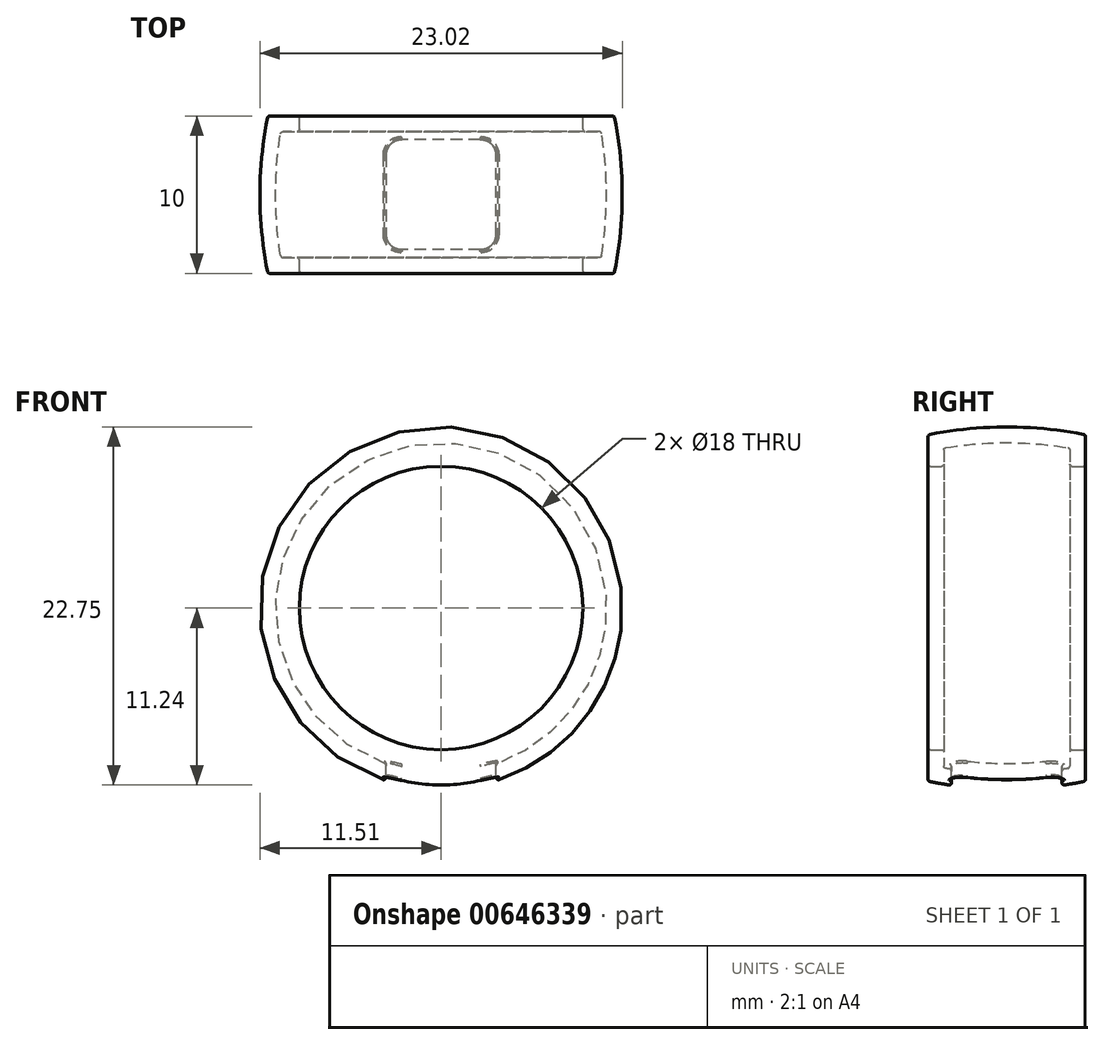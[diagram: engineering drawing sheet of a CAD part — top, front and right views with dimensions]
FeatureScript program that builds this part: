
annotation { "Feature Type Name" : "Feature", "Feature Type Description" : "" }
export const myFeature = defineFeature(function(context is Context, id is Id, definition is map)
    precondition{}
    {
        {
            var Q0;
            Q0=qCreatedBy(makeId("Top.planeOp"),FACE);
            var sketch = newSketch(context, id + "F0", { "sketchPlane" : qUnion([Q0])});
            skLineSegment(sketch, "E0", {"start": v(0, 0) * mm, "end": v(-9, 0) * mm, "construction": true});
            skLineSegment(sketch, "E1", {"start": v(-9, 5) * mm, "end": v(-9, -5) * mm});
            skLineSegment(sketch, "E2", {"start": v(-9, 5) * mm, "end": v(-11, 5) * mm});
            skLineSegment(sketch, "E3", {"start": v(-9, -5) * mm, "end": v(-11, -5) * mm});
            skArc(sketch, "E4", {"start": v(-11, 5) * mm, "mid": v(-11.5, 0) * mm, "end": v(-11, -5) * mm});
            skLineSegment(sketch, "E5", {"start": v(0, 0) * mm, "end": v(0, -17) * mm, "construction": true});
            skSolve(sketch);
        }
        {
            var Q0;
            Q0=makeQuery(id+"F0.imprint","IMPRINT",FACE,{"disambiguationData":[TD([[makeQuery(id+"F0.imprint","IMPRINT",EDGE,{"derivedFrom":sQuery(id+"F0.wireOp",EDGE,"E1")}),-1.0]])]});
            var Q1;
            Q1=sQuery(id+"F0.wireOp",EDGE,"E5");
            revolve(context, id + "F1", {"entities" : qUnion([Q0]), "axis" : qUnion([Q1]), "revolveType" : RevolveType.FULL});
        }
        {
            var Q0;
            Q0=makeQuery(id+"F1.opRevolve","SWEPT_FACE",FACE,{"disambiguationData":[OSD([sQuery(id+"F0.wireOp",EDGE,"E1")])]});
            shell(context, id + "F2", {"entities" : qUnion([Q0]), "thickness" : 1 * mm});
        }
        {
            var Q0;
            Q0=makeQuery(id+"F1.opRevolve","SWEPT_EDGE",EDGE,{"disambiguationData":[OSD([sQuery(id+"F0.wireOp",EDGE,"E1"),sQuery(id+"F0.wireOp",EDGE,"E2")])]});
            var Q1;
            Q1=makeQuery(id+"F1.opRevolve","SWEPT_EDGE",EDGE,{"disambiguationData":[OSD([sQuery(id+"F0.wireOp",EDGE,"E2"),sQuery(id+"F0.wireOp",EDGE,"E4")])]});
            var Q2;
            Q2=makeQuery(id+"F2.opShell","OFFSET_FACE",FACE,{"disambiguationData":[OSD([sQuery(id+"F0.wireOp",EDGE,"E1")])]});
            var Q3;
            Q3=makeQuery(id+"F1.opRevolve","SWEPT_FACE",FACE,{"disambiguationData":[OSD([sQuery(id+"F0.wireOp",EDGE,"E2")])]});
            var Q4;
            Q4=makeQuery(id+"F1.opRevolve","SWEPT_EDGE",EDGE,{"disambiguationData":[OSD([sQuery(id+"F0.wireOp",EDGE,"E3"),sQuery(id+"F0.wireOp",EDGE,"E4")])]});
            var Q5;
            Q5=makeQuery(id+"F2.opShell","OFFSET_EDGE",EDGE,{"disambiguationData":[OSD([sQuery(id+"F0.wireOp",EDGE,"E1"),sQuery(id+"F0.wireOp",EDGE,"E2")])]});
            var Q6;
            Q6=makeQuery(id+"F1.opRevolve","SWEPT_FACE",FACE,{"disambiguationData":[OSD([sQuery(id+"F0.wireOp",EDGE,"E3")])]});
            var Q7;
            Q7=makeQuery(id+"F1.opRevolve","SWEPT_EDGE",EDGE,{"disambiguationData":[OSD([sQuery(id+"F0.wireOp",EDGE,"E1"),sQuery(id+"F0.wireOp",EDGE,"E3")])]});
            var Q8;
            Q8=makeQuery(id+"F2.opShell","OFFSET_EDGE",EDGE,{"disambiguationData":[OSD([sQuery(id+"F0.wireOp",EDGE,"E1"),sQuery(id+"F0.wireOp",EDGE,"E3")])]});
            var Q9;
            Q9=makeQuery(id+"F2.opShell","OFFSET_FACE",FACE,{"disambiguationData":[OSD([sQuery(id+"F0.wireOp",EDGE,"E2")])]});
            var Q10;
            Q10=makeQuery(id+"F2.opShell","OFFSET_EDGE",EDGE,{"disambiguationData":[OSD([sQuery(id+"F0.wireOp",EDGE,"E2"),sQuery(id+"F0.wireOp",EDGE,"E4")])]});
            var Q11;
            Q11=makeQuery(id+"F2.opShell","OFFSET_FACE",FACE,{"disambiguationData":[OSD([sQuery(id+"F0.wireOp",EDGE,"E3")])]});
            var Q12;
            Q12=makeQuery(id+"F2.opShell","OFFSET_EDGE",EDGE,{"disambiguationData":[OSD([sQuery(id+"F0.wireOp",EDGE,"E3"),sQuery(id+"F0.wireOp",EDGE,"E4")])]});
            var Q13;
            Q13=makeQuery(id+"F2.opShell","OFFSET_FACE",FACE,{"disambiguationData":[OSD([sQuery(id+"F0.wireOp",EDGE,"E4")])]});
            var Q14;
            Q14=makeQuery(id+"F1.opRevolve","SWEPT_FACE",FACE,{"disambiguationData":[OSD([sQuery(id+"F0.wireOp",EDGE,"E1")])]});
            var Q15;
            Q15=makeQuery(id+"F1.opRevolve","SWEPT_FACE",FACE,{"disambiguationData":[OSD([sQuery(id+"F0.wireOp",EDGE,"E4")])]});
            fillet(context, id + "F3", {"entities" : qUnion([Q0, Q1, Q2, Q3, Q4, Q5, Q6, Q7, Q8, Q9, Q10, Q11, Q12, Q13, Q14, Q15]), "radius" : 0.15 * mm, "tangentPropagation" : true, "allowEdgeOverflow" : false});
        }
        {
            var Q0;
            Q0=qCreatedBy(makeId("Top.planeOp"),FACE);
            var sketch = newSketch(context, id + "F4", { "sketchPlane" : qUnion([Q0])});
            skLineSegment(sketch, "E6.bottom", {"start": v(2.5, 3.5) * mm, "end": v(-2.5, 3.5) * mm});
            skLineSegment(sketch, "E6.top", {"start": v(2.5, -3.5) * mm, "end": v(-2.5, -3.5) * mm});
            skLineSegment(sketch, "E6.left", {"start": v(3.5, 2.5) * mm, "end": v(3.5, -2.5) * mm});
            skLineSegment(sketch, "E6.right", {"start": v(-3.5, 2.5) * mm, "end": v(-3.5, -2.5) * mm});
            skPoint(sketch, "E6.middle", {"position": v(0, 0) * mm});
            skPoint(sketch, "E7.visualSharp", {"position": v(-3.5, 3.5) * mm});
            skArc(sketch, "E7.filletArc", {"start": v(-2.5, 3.5) * mm, "mid": v(-3.2, 3.2) * mm, "end": v(-3.5, 2.5) * mm});
            skPoint(sketch, "E8.visualSharp", {"position": v(3.5, 3.5) * mm});
            skArc(sketch, "E8.filletArc", {"start": v(3.5, 2.5) * mm, "mid": v(3.2, 3.2) * mm, "end": v(2.5, 3.5) * mm});
            skPoint(sketch, "E9.visualSharp", {"position": v(3.5, -3.5) * mm});
            skArc(sketch, "E9.filletArc", {"start": v(2.5, -3.5) * mm, "mid": v(3.2, -3.2) * mm, "end": v(3.5, -2.5) * mm});
            skPoint(sketch, "E10.visualSharp", {"position": v(-3.5, -3.5) * mm});
            skArc(sketch, "E10.filletArc", {"start": v(-3.5, -2.5) * mm, "mid": v(-3.2, -3.2) * mm, "end": v(-2.5, -3.5) * mm});
            skSolve(sketch);
        }
        {
            var Q0;
            Q0=makeQuery(id+"F4.imprint","IMPRINT",FACE,{"disambiguationData":[TD([[makeQuery(id+"F4.imprint","IMPRINT",EDGE,{"derivedFrom":sQuery(id+"F4.wireOp",EDGE,"E6.bottom")}),1.0]])]});
            extrude(context, id + "F5", {"entities" : qUnion([Q0]), "operationType" : NewBodyOperationType.REMOVE, "endBound" : BoundingType.THROUGH_ALL, "oppositeDirection" : true, "depth" : 25 * mm, "offsetDistance" : 25 * mm});
        }
        {
            var Q0;
            {var subQ0=sQuery(id+"F0.wireOp",EDGE,"E3");var subQ1=sQuery(id+"F0.wireOp",EDGE,"E1");Q0=makeQuery(id+"F3.opFillet","BLEND_FACE",FACE,{"disambiguationData":[OSD([subQ1,subQ0]),TDD([makeQuery(id+"F1.opRevolve","SWEPT_EDGE",EDGE,{"disambiguationData":[OSD([subQ1,subQ0])]})])]});}
            var Q1;
            {var subQ0=sQuery(id+"F0.wireOp",EDGE,"E3");var subQ1=sQuery(id+"F0.wireOp",EDGE,"E1");Q1=makeQuery(id+"F3.opFillet","BLEND_FACE",FACE,{"disambiguationData":[OSD([subQ1,subQ0]),TDD([makeQuery(id+"F2.opShell","OFFSET_EDGE",EDGE,{"disambiguationData":[OSD([subQ1,subQ0])]})])]});}
            var Q2;
            {var subQ0=sQuery(id+"F0.wireOp",EDGE,"E2");var subQ1=sQuery(id+"F0.wireOp",EDGE,"E1");Q2=makeQuery(id+"F3.opFillet","BLEND_FACE",FACE,{"disambiguationData":[OSD([subQ1,subQ0]),TDD([makeQuery(id+"F2.opShell","OFFSET_EDGE",EDGE,{"disambiguationData":[OSD([subQ1,subQ0])]})])]});}
            var Q3;
            {var subQ0=sQuery(id+"F0.wireOp",EDGE,"E1");Q3=makeQuery(id+"F3.opFillet","BLEND_EDGE",EDGE,{"blendedFrom":[makeQuery(id+"F1.opRevolve","SWEPT_EDGE",EDGE,{"disambiguationData":[OSD([subQ0,sQuery(id+"F0.wireOp",EDGE,"E2")])]}),makeQuery(id+"F2.opShell","OFFSET_FACE",FACE,{"disambiguationData":[OSD([subQ0])]})],"blendedInto":[makeQuery(id+"F2.opShell","OFFSET_FACE",FACE,{"disambiguationData":[OSD([subQ0])]})]});}
            var Q4;
            {var subQ0=sQuery(id+"F0.wireOp",EDGE,"E4");Q4=makeQuery(id+"F3.opFillet","BLEND_EDGE",EDGE,{"blendedFrom":[makeQuery(id+"F1.opRevolve","SWEPT_EDGE",EDGE,{"disambiguationData":[OSD([sQuery(id+"F0.wireOp",EDGE,"E2"),subQ0])]}),makeQuery(id+"F1.opRevolve","SWEPT_FACE",FACE,{"disambiguationData":[OSD([subQ0])]})],"blendedInto":[makeQuery(id+"F1.opRevolve","SWEPT_FACE",FACE,{"disambiguationData":[OSD([subQ0])]})]});}
            var Q5;
            {var subQ0=sQuery(id+"F0.wireOp",EDGE,"E4");var subQ1=sQuery(id+"F0.wireOp",EDGE,"E3");Q5=makeQuery(id+"F3.opFillet","BLEND_FACE",FACE,{"disambiguationData":[OSD([subQ1,subQ0]),TDD([makeQuery(id+"F1.opRevolve","SWEPT_EDGE",EDGE,{"disambiguationData":[OSD([subQ1,subQ0])]})])]});}
            var Q6;
            {var subQ0=sQuery(id+"F0.wireOp",EDGE,"E1");Q6=makeQuery(id+"F3.opFillet","BLEND_EDGE",EDGE,{"blendedFrom":[makeQuery(id+"F1.opRevolve","SWEPT_EDGE",EDGE,{"disambiguationData":[OSD([subQ0,sQuery(id+"F0.wireOp",EDGE,"E3")])]}),makeQuery(id+"F1.opRevolve","SWEPT_FACE",FACE,{"disambiguationData":[OSD([subQ0])]})],"blendedInto":[makeQuery(id+"F1.opRevolve","SWEPT_FACE",FACE,{"disambiguationData":[OSD([subQ0])]})]});}
            var Q7;
            {var subQ0=sQuery(id+"F0.wireOp",EDGE,"E4");var subQ1=sQuery(id+"F0.wireOp",EDGE,"E2");Q7=makeQuery(id+"F3.opFillet","BLEND_FACE",FACE,{"disambiguationData":[OSD([subQ1,subQ0]),TDD([makeQuery(id+"F1.opRevolve","SWEPT_EDGE",EDGE,{"disambiguationData":[OSD([subQ1,subQ0])]})])]});}
            var Q8;
            {var subQ0=sQuery(id+"F0.wireOp",EDGE,"E3");Q8=makeQuery(id+"F3.opFillet","BLEND_EDGE",EDGE,{"blendedFrom":[makeQuery(id+"F1.opRevolve","SWEPT_EDGE",EDGE,{"disambiguationData":[OSD([subQ0,sQuery(id+"F0.wireOp",EDGE,"E4")])]}),makeQuery(id+"F1.opRevolve","SWEPT_FACE",FACE,{"disambiguationData":[OSD([subQ0])]})],"blendedInto":[makeQuery(id+"F1.opRevolve","SWEPT_FACE",FACE,{"disambiguationData":[OSD([subQ0])]})]});}
            var Q9;
            {var subQ0=sQuery(id+"F0.wireOp",EDGE,"E3");Q9=makeQuery(id+"F3.opFillet","BLEND_EDGE",EDGE,{"blendedFrom":[makeQuery(id+"F1.opRevolve","SWEPT_EDGE",EDGE,{"disambiguationData":[OSD([sQuery(id+"F0.wireOp",EDGE,"E1"),subQ0])]}),makeQuery(id+"F1.opRevolve","SWEPT_FACE",FACE,{"disambiguationData":[OSD([subQ0])]})],"blendedInto":[makeQuery(id+"F1.opRevolve","SWEPT_FACE",FACE,{"disambiguationData":[OSD([subQ0])]})]});}
            var Q10;
            {var subQ0=sQuery(id+"F0.wireOp",EDGE,"E2");var subQ1=sQuery(id+"F0.wireOp",EDGE,"E1");Q10=makeQuery(id+"F3.opFillet","BLEND_FACE",FACE,{"disambiguationData":[OSD([subQ1,subQ0]),TDD([makeQuery(id+"F1.opRevolve","SWEPT_EDGE",EDGE,{"disambiguationData":[OSD([subQ1,subQ0])]})])]});}
            var Q11;
            {var subQ0=sQuery(id+"F0.wireOp",EDGE,"E4");Q11=makeQuery(id+"F3.opFillet","BLEND_EDGE",EDGE,{"blendedFrom":[makeQuery(id+"F2.opShell","OFFSET_EDGE",EDGE,{"disambiguationData":[OSD([sQuery(id+"F0.wireOp",EDGE,"E2"),subQ0])]}),makeQuery(id+"F2.opShell","OFFSET_FACE",FACE,{"disambiguationData":[OSD([subQ0])]})],"blendedInto":[makeQuery(id+"F2.opShell","OFFSET_FACE",FACE,{"disambiguationData":[OSD([subQ0])]})]});}
            var Q12;
            Q12=makeQuery(id+"F1.opRevolve","SWEPT_FACE",FACE,{"disambiguationData":[OSD([sQuery(id+"F0.wireOp",EDGE,"E1")])]});
            var Q13;
            Q13=makeQuery(id+"F5.boolean.opBoolean","COPY",FACE,{"derivedFrom":makeQuery(id+"F5.opExtrude","SWEPT_FACE",FACE,{"disambiguationData":[OSD([sQuery(id+"F4.wireOp",EDGE,"E10.filletArc")])]})});
            var Q14;
            {var subQ0=sQuery(id+"F0.wireOp",EDGE,"E1");Q14=makeQuery(id+"F3.opFillet","BLEND_EDGE",EDGE,{"blendedFrom":[makeQuery(id+"F2.opShell","OFFSET_EDGE",EDGE,{"disambiguationData":[OSD([subQ0,sQuery(id+"F0.wireOp",EDGE,"E3")])]}),makeQuery(id+"F1.opRevolve","SWEPT_FACE",FACE,{"disambiguationData":[OSD([subQ0])]})],"blendedInto":[makeQuery(id+"F1.opRevolve","SWEPT_FACE",FACE,{"disambiguationData":[OSD([subQ0])]})]});}
            var Q15;
            Q15=makeQuery(id+"F2.opShell","OFFSET_FACE",FACE,{"disambiguationData":[OSD([sQuery(id+"F0.wireOp",EDGE,"E1")])]});
            var Q16;
            Q16=makeQuery(id+"F5.boolean.opBoolean","COPY",FACE,{"derivedFrom":makeQuery(id+"F5.opExtrude","SWEPT_FACE",FACE,{"disambiguationData":[OSD([sQuery(id+"F4.wireOp",EDGE,"E6.right")])]})});
            var Q17;
            {var subQ0=sQuery(id+"F0.wireOp",EDGE,"E2");Q17=makeQuery(id+"F3.opFillet","BLEND_EDGE",EDGE,{"blendedFrom":[makeQuery(id+"F2.opShell","OFFSET_EDGE",EDGE,{"disambiguationData":[OSD([subQ0,sQuery(id+"F0.wireOp",EDGE,"E4")])]}),makeQuery(id+"F2.opShell","OFFSET_FACE",FACE,{"disambiguationData":[OSD([subQ0])]})],"blendedInto":[makeQuery(id+"F2.opShell","OFFSET_FACE",FACE,{"disambiguationData":[OSD([subQ0])]})]});}
            var Q18;
            Q18=makeQuery(id+"F2.opShell","OFFSET_FACE",FACE,{"disambiguationData":[OSD([sQuery(id+"F0.wireOp",EDGE,"E2")])]});
            var Q19;
            Q19=makeQuery(id+"F5.boolean.opBoolean","COPY",FACE,{"derivedFrom":makeQuery(id+"F5.opExtrude","SWEPT_FACE",FACE,{"disambiguationData":[OSD([sQuery(id+"F4.wireOp",EDGE,"E6.bottom")])]})});
            var Q20;
            Q20=makeQuery(id+"F5.boolean.opBoolean","INTERSECT",EDGE,{"derivedFrom":[makeQuery(id+"F2.opShell","OFFSET_FACE",FACE,{"disambiguationData":[OSD([sQuery(id+"F0.wireOp",EDGE,"E4")])]}),makeQuery(id+"F5.opExtrude","SWEPT_FACE",FACE,{"disambiguationData":[OSD([sQuery(id+"F4.wireOp",EDGE,"E6.right")])]})]});
            var Q21;
            {var subQ0=sQuery(id+"F0.wireOp",EDGE,"E1");Q21=makeQuery(id+"F3.opFillet","BLEND_EDGE",EDGE,{"blendedFrom":[makeQuery(id+"F2.opShell","OFFSET_EDGE",EDGE,{"disambiguationData":[OSD([subQ0,sQuery(id+"F0.wireOp",EDGE,"E2")])]}),makeQuery(id+"F2.opShell","OFFSET_FACE",FACE,{"disambiguationData":[OSD([subQ0])]})],"blendedInto":[makeQuery(id+"F2.opShell","OFFSET_FACE",FACE,{"disambiguationData":[OSD([subQ0])]})]});}
            var Q22;
            Q22=makeQuery(id+"F5.boolean.opBoolean","INTERSECT",EDGE,{"derivedFrom":[makeQuery(id+"F1.opRevolve","SWEPT_FACE",FACE,{"disambiguationData":[OSD([sQuery(id+"F0.wireOp",EDGE,"E4")])]}),makeQuery(id+"F5.opExtrude","SWEPT_FACE",FACE,{"disambiguationData":[OSD([sQuery(id+"F4.wireOp",EDGE,"E6.right")])]})]});
            var Q23;
            Q23=makeQuery(id+"F5.boolean.opBoolean","COPY",FACE,{"derivedFrom":makeQuery(id+"F5.opExtrude","SWEPT_FACE",FACE,{"disambiguationData":[OSD([sQuery(id+"F4.wireOp",EDGE,"E7.filletArc")])]})});
            var Q24;
            {var subQ0=sQuery(id+"F0.wireOp",EDGE,"E4");Q24=makeQuery(id+"F3.opFillet","BLEND_EDGE",EDGE,{"blendedFrom":[makeQuery(id+"F1.opRevolve","SWEPT_EDGE",EDGE,{"disambiguationData":[OSD([sQuery(id+"F0.wireOp",EDGE,"E3"),subQ0])]}),makeQuery(id+"F1.opRevolve","SWEPT_FACE",FACE,{"disambiguationData":[OSD([subQ0])]})],"blendedInto":[makeQuery(id+"F1.opRevolve","SWEPT_FACE",FACE,{"disambiguationData":[OSD([subQ0])]})]});}
            var Q25;
            Q25=makeQuery(id+"F1.opRevolve","SWEPT_FACE",FACE,{"disambiguationData":[OSD([sQuery(id+"F0.wireOp",EDGE,"E3")])]});
            var Q26;
            {var subQ0=sQuery(id+"F0.wireOp",EDGE,"E2");Q26=makeQuery(id+"F3.opFillet","BLEND_EDGE",EDGE,{"blendedFrom":[makeQuery(id+"F2.opShell","OFFSET_EDGE",EDGE,{"disambiguationData":[OSD([sQuery(id+"F0.wireOp",EDGE,"E1"),subQ0])]}),makeQuery(id+"F2.opShell","OFFSET_FACE",FACE,{"disambiguationData":[OSD([subQ0])]})],"blendedInto":[makeQuery(id+"F2.opShell","OFFSET_FACE",FACE,{"disambiguationData":[OSD([subQ0])]})]});}
            var Q27;
            {var subQ0=sQuery(id+"F0.wireOp",EDGE,"E4");var subQ1=sQuery(id+"F0.wireOp",EDGE,"E2");Q27=makeQuery(id+"F3.opFillet","BLEND_FACE",FACE,{"disambiguationData":[OSD([subQ1,subQ0]),TDD([makeQuery(id+"F2.opShell","OFFSET_EDGE",EDGE,{"disambiguationData":[OSD([subQ1,subQ0])]})])]});}
            var Q28;
            Q28=makeQuery(id+"F5.boolean.opBoolean","INTERSECT",EDGE,{"derivedFrom":[makeQuery(id+"F2.opShell","OFFSET_FACE",FACE,{"disambiguationData":[OSD([sQuery(id+"F0.wireOp",EDGE,"E4")])]}),makeQuery(id+"F5.opExtrude","SWEPT_FACE",FACE,{"disambiguationData":[OSD([sQuery(id+"F4.wireOp",EDGE,"E6.bottom")])]})]});
            var Q29;
            Q29=makeQuery(id+"F5.boolean.opBoolean","INTERSECT",EDGE,{"derivedFrom":[makeQuery(id+"F1.opRevolve","SWEPT_FACE",FACE,{"disambiguationData":[OSD([sQuery(id+"F0.wireOp",EDGE,"E4")])]}),makeQuery(id+"F5.opExtrude","SWEPT_FACE",FACE,{"disambiguationData":[OSD([sQuery(id+"F4.wireOp",EDGE,"E6.bottom")])]})]});
            var Q30;
            Q30=makeQuery(id+"Fd9uYAkPvKm23FF_1.3.F5.boolean.opBoolean","INTERSECT",EDGE,{"derivedFrom":[makeQuery(id+"F1.opRevolve","SWEPT_FACE",FACE,{"disambiguationData":[OSD([sQuery(id+"F0.wireOp",EDGE,"E4")])]}),makeQuery(id+"Fd9uYAkPvKm23FF_1.3.F5.opExtrude","SWEPT_FACE",FACE,{"disambiguationData":[OSD([sQuery(id+"F4.wireOp",EDGE,"E6.top")])]})]});
            var Q31;
            Q31=makeQuery(id+"Fd9uYAkPvKm23FF_1.3.F5.boolean.opBoolean","INTERSECT",EDGE,{"derivedFrom":[makeQuery(id+"F2.opShell","OFFSET_FACE",FACE,{"disambiguationData":[OSD([sQuery(id+"F0.wireOp",EDGE,"E4")])]}),makeQuery(id+"Fd9uYAkPvKm23FF_1.3.F5.opExtrude","SWEPT_FACE",FACE,{"disambiguationData":[OSD([sQuery(id+"F4.wireOp",EDGE,"E6.bottom")])]})]});
            var Q32;
            Q32=makeQuery(id+"Fd9uYAkPvKm23FF_1.3.F5.boolean.opBoolean","INTERSECT",EDGE,{"derivedFrom":[makeQuery(id+"F1.opRevolve","SWEPT_FACE",FACE,{"disambiguationData":[OSD([sQuery(id+"F0.wireOp",EDGE,"E4")])]}),makeQuery(id+"Fd9uYAkPvKm23FF_1.3.F5.opExtrude","SWEPT_FACE",FACE,{"disambiguationData":[OSD([sQuery(id+"F4.wireOp",EDGE,"E6.bottom")])]})]});
            var Q33;
            Q33=makeQuery(id+"Fd9uYAkPvKm23FF_1.3.F5.boolean.opBoolean","COPY",FACE,{"derivedFrom":makeQuery(id+"Fd9uYAkPvKm23FF_1.3.F5.opExtrude","SWEPT_FACE",FACE,{"disambiguationData":[OSD([sQuery(id+"F4.wireOp",EDGE,"E10.filletArc")])]})});
            var Q34;
            Q34=makeQuery(id+"Fd9uYAkPvKm23FF_1.3.F5.boolean.opBoolean","COPY",FACE,{"derivedFrom":makeQuery(id+"Fd9uYAkPvKm23FF_1.3.F5.opExtrude","SWEPT_FACE",FACE,{"disambiguationData":[OSD([sQuery(id+"F4.wireOp",EDGE,"E9.filletArc")])]})});
            var Q35;
            Q35=makeQuery(id+"Fd9uYAkPvKm23FF_1.3.F5.boolean.opBoolean","COPY",FACE,{"derivedFrom":makeQuery(id+"Fd9uYAkPvKm23FF_1.3.F5.opExtrude","SWEPT_FACE",FACE,{"disambiguationData":[OSD([sQuery(id+"F4.wireOp",EDGE,"E8.filletArc")])]})});
            var Q36;
            Q36=makeQuery(id+"Fd9uYAkPvKm23FF_1.3.F5.boolean.opBoolean","COPY",FACE,{"derivedFrom":makeQuery(id+"Fd9uYAkPvKm23FF_1.3.F5.opExtrude","SWEPT_FACE",FACE,{"disambiguationData":[OSD([sQuery(id+"F4.wireOp",EDGE,"E7.filletArc")])]})});
            var Q37;
            Q37=makeQuery(id+"Fd9uYAkPvKm23FF_1.3.F5.boolean.opBoolean","COPY",FACE,{"derivedFrom":makeQuery(id+"Fd9uYAkPvKm23FF_1.3.F5.opExtrude","SWEPT_FACE",FACE,{"disambiguationData":[OSD([sQuery(id+"F4.wireOp",EDGE,"E6.right")])]})});
            var Q38;
            Q38=makeQuery(id+"Fd9uYAkPvKm23FF_1.3.F5.boolean.opBoolean","COPY",FACE,{"derivedFrom":makeQuery(id+"Fd9uYAkPvKm23FF_1.3.F5.opExtrude","SWEPT_FACE",FACE,{"disambiguationData":[OSD([sQuery(id+"F4.wireOp",EDGE,"E6.left")])]})});
            var Q39;
            Q39=makeQuery(id+"Fd9uYAkPvKm23FF_1.3.F5.boolean.opBoolean","COPY",FACE,{"derivedFrom":makeQuery(id+"Fd9uYAkPvKm23FF_1.3.F5.opExtrude","SWEPT_FACE",FACE,{"disambiguationData":[OSD([sQuery(id+"F4.wireOp",EDGE,"E6.bottom")])]})});
            var Q40;
            Q40=makeQuery(id+"Fd9uYAkPvKm23FF_1.3.F5.boolean.opBoolean","INTERSECT",EDGE,{"derivedFrom":[makeQuery(id+"F1.opRevolve","SWEPT_FACE",FACE,{"disambiguationData":[OSD([sQuery(id+"F0.wireOp",EDGE,"E4")])]}),makeQuery(id+"Fd9uYAkPvKm23FF_1.3.F5.opExtrude","SWEPT_FACE",FACE,{"disambiguationData":[OSD([sQuery(id+"F4.wireOp",EDGE,"E6.right")])]})]});
            var Q41;
            Q41=makeQuery(id+"Fd9uYAkPvKm23FF_1.2.F5.boolean.opBoolean","INTERSECT",EDGE,{"derivedFrom":[makeQuery(id+"F1.opRevolve","SWEPT_FACE",FACE,{"disambiguationData":[OSD([sQuery(id+"F0.wireOp",EDGE,"E4")])]}),makeQuery(id+"Fd9uYAkPvKm23FF_1.2.F5.opExtrude","SWEPT_FACE",FACE,{"disambiguationData":[OSD([sQuery(id+"F4.wireOp",EDGE,"E6.left")])]})]});
            var Q42;
            Q42=makeQuery(id+"Fd9uYAkPvKm23FF_1.2.F5.boolean.opBoolean","INTERSECT",EDGE,{"derivedFrom":[makeQuery(id+"F1.opRevolve","SWEPT_FACE",FACE,{"disambiguationData":[OSD([sQuery(id+"F0.wireOp",EDGE,"E4")])]}),makeQuery(id+"Fd9uYAkPvKm23FF_1.2.F5.opExtrude","SWEPT_FACE",FACE,{"disambiguationData":[OSD([sQuery(id+"F4.wireOp",EDGE,"E6.top")])]})]});
            var Q43;
            Q43=makeQuery(id+"Fd9uYAkPvKm23FF_1.2.F5.boolean.opBoolean","INTERSECT",EDGE,{"derivedFrom":[makeQuery(id+"F2.opShell","OFFSET_FACE",FACE,{"disambiguationData":[OSD([sQuery(id+"F0.wireOp",EDGE,"E4")])]}),makeQuery(id+"Fd9uYAkPvKm23FF_1.2.F5.opExtrude","SWEPT_FACE",FACE,{"disambiguationData":[OSD([sQuery(id+"F4.wireOp",EDGE,"E6.bottom")])]})]});
            var Q44;
            Q44=makeQuery(id+"Fd9uYAkPvKm23FF_1.2.F5.boolean.opBoolean","INTERSECT",EDGE,{"derivedFrom":[makeQuery(id+"F1.opRevolve","SWEPT_FACE",FACE,{"disambiguationData":[OSD([sQuery(id+"F0.wireOp",EDGE,"E4")])]}),makeQuery(id+"Fd9uYAkPvKm23FF_1.2.F5.opExtrude","SWEPT_FACE",FACE,{"disambiguationData":[OSD([sQuery(id+"F4.wireOp",EDGE,"E6.bottom")])]})]});
            var Q45;
            Q45=makeQuery(id+"Fd9uYAkPvKm23FF_1.2.F5.boolean.opBoolean","COPY",FACE,{"derivedFrom":makeQuery(id+"Fd9uYAkPvKm23FF_1.2.F5.opExtrude","SWEPT_FACE",FACE,{"disambiguationData":[OSD([sQuery(id+"F4.wireOp",EDGE,"E9.filletArc")])]})});
            var Q46;
            Q46=makeQuery(id+"Fd9uYAkPvKm23FF_1.2.F5.boolean.opBoolean","COPY",FACE,{"derivedFrom":makeQuery(id+"Fd9uYAkPvKm23FF_1.2.F5.opExtrude","SWEPT_FACE",FACE,{"disambiguationData":[OSD([sQuery(id+"F4.wireOp",EDGE,"E8.filletArc")])]})});
            var Q47;
            Q47=makeQuery(id+"Fd9uYAkPvKm23FF_1.2.F5.boolean.opBoolean","COPY",FACE,{"derivedFrom":makeQuery(id+"Fd9uYAkPvKm23FF_1.2.F5.opExtrude","SWEPT_FACE",FACE,{"disambiguationData":[OSD([sQuery(id+"F4.wireOp",EDGE,"E6.right")])]})});
            var Q48;
            Q48=makeQuery(id+"Fd9uYAkPvKm23FF_1.2.F5.boolean.opBoolean","COPY",FACE,{"derivedFrom":makeQuery(id+"Fd9uYAkPvKm23FF_1.2.F5.opExtrude","SWEPT_FACE",FACE,{"disambiguationData":[OSD([sQuery(id+"F4.wireOp",EDGE,"E6.top")])]})});
            var Q49;
            Q49=makeQuery(id+"Fd9uYAkPvKm23FF_1.2.F5.boolean.opBoolean","COPY",FACE,{"derivedFrom":makeQuery(id+"Fd9uYAkPvKm23FF_1.2.F5.opExtrude","SWEPT_FACE",FACE,{"disambiguationData":[OSD([sQuery(id+"F4.wireOp",EDGE,"E6.bottom")])]})});
            var Q50;
            Q50=makeQuery(id+"Fd9uYAkPvKm23FF_1.2.F5.boolean.opBoolean","INTERSECT",EDGE,{"derivedFrom":[makeQuery(id+"F2.opShell","OFFSET_FACE",FACE,{"disambiguationData":[OSD([sQuery(id+"F0.wireOp",EDGE,"E4")])]}),makeQuery(id+"Fd9uYAkPvKm23FF_1.2.F5.opExtrude","SWEPT_FACE",FACE,{"disambiguationData":[OSD([sQuery(id+"F4.wireOp",EDGE,"E6.right")])]})]});
            var Q51;
            Q51=makeQuery(id+"Fd9uYAkPvKm23FF_1.2.F5.boolean.opBoolean","INTERSECT",EDGE,{"derivedFrom":[makeQuery(id+"F1.opRevolve","SWEPT_FACE",FACE,{"disambiguationData":[OSD([sQuery(id+"F0.wireOp",EDGE,"E4")])]}),makeQuery(id+"Fd9uYAkPvKm23FF_1.2.F5.opExtrude","SWEPT_FACE",FACE,{"disambiguationData":[OSD([sQuery(id+"F4.wireOp",EDGE,"E6.right")])]})]});
            var Q52;
            Q52=makeQuery(id+"Fd9uYAkPvKm23FF_1.1.F5.boolean.opBoolean","INTERSECT",EDGE,{"derivedFrom":[makeQuery(id+"F1.opRevolve","SWEPT_FACE",FACE,{"disambiguationData":[OSD([sQuery(id+"F0.wireOp",EDGE,"E4")])]}),makeQuery(id+"Fd9uYAkPvKm23FF_1.1.F5.opExtrude","SWEPT_FACE",FACE,{"disambiguationData":[OSD([sQuery(id+"F4.wireOp",EDGE,"E6.left")])]})]});
            var Q53;
            Q53=makeQuery(id+"Fd9uYAkPvKm23FF_1.1.F5.boolean.opBoolean","INTERSECT",EDGE,{"derivedFrom":[makeQuery(id+"F1.opRevolve","SWEPT_FACE",FACE,{"disambiguationData":[OSD([sQuery(id+"F0.wireOp",EDGE,"E4")])]}),makeQuery(id+"Fd9uYAkPvKm23FF_1.1.F5.opExtrude","SWEPT_FACE",FACE,{"disambiguationData":[OSD([sQuery(id+"F4.wireOp",EDGE,"E6.top")])]})]});
            var Q54;
            Q54=makeQuery(id+"Fd9uYAkPvKm23FF_1.1.F5.boolean.opBoolean","INTERSECT",EDGE,{"derivedFrom":[makeQuery(id+"F1.opRevolve","SWEPT_FACE",FACE,{"disambiguationData":[OSD([sQuery(id+"F0.wireOp",EDGE,"E4")])]}),makeQuery(id+"Fd9uYAkPvKm23FF_1.1.F5.opExtrude","SWEPT_FACE",FACE,{"disambiguationData":[OSD([sQuery(id+"F4.wireOp",EDGE,"E6.bottom")])]})]});
            var Q55;
            Q55=makeQuery(id+"Fd9uYAkPvKm23FF_1.1.F5.boolean.opBoolean","COPY",FACE,{"derivedFrom":makeQuery(id+"Fd9uYAkPvKm23FF_1.1.F5.opExtrude","SWEPT_FACE",FACE,{"disambiguationData":[OSD([sQuery(id+"F4.wireOp",EDGE,"E7.filletArc")])]})});
            var Q56;
            Q56=makeQuery(id+"Fd9uYAkPvKm23FF_1.1.F5.boolean.opBoolean","COPY",FACE,{"derivedFrom":makeQuery(id+"Fd9uYAkPvKm23FF_1.1.F5.opExtrude","SWEPT_FACE",FACE,{"disambiguationData":[OSD([sQuery(id+"F4.wireOp",EDGE,"E6.right")])]})});
            var Q57;
            Q57=makeQuery(id+"Fd9uYAkPvKm23FF_1.1.F5.boolean.opBoolean","COPY",FACE,{"derivedFrom":makeQuery(id+"Fd9uYAkPvKm23FF_1.1.F5.opExtrude","SWEPT_FACE",FACE,{"disambiguationData":[OSD([sQuery(id+"F4.wireOp",EDGE,"E6.top")])]})});
            var Q58;
            Q58=makeQuery(id+"Fd9uYAkPvKm23FF_1.1.F5.boolean.opBoolean","COPY",FACE,{"derivedFrom":makeQuery(id+"Fd9uYAkPvKm23FF_1.1.F5.opExtrude","SWEPT_FACE",FACE,{"disambiguationData":[OSD([sQuery(id+"F4.wireOp",EDGE,"E6.bottom")])]})});
            var Q59;
            Q59=makeQuery(id+"Fd9uYAkPvKm23FF_1.1.F5.boolean.opBoolean","INTERSECT",EDGE,{"derivedFrom":[makeQuery(id+"F1.opRevolve","SWEPT_FACE",FACE,{"disambiguationData":[OSD([sQuery(id+"F0.wireOp",EDGE,"E4")])]}),makeQuery(id+"Fd9uYAkPvKm23FF_1.1.F5.opExtrude","SWEPT_FACE",FACE,{"disambiguationData":[OSD([sQuery(id+"F4.wireOp",EDGE,"E6.right")])]})]});
            var Q60;
            Q60=makeQuery(id+"Fd9uYAkPvKm23FF_1.3.F5.boolean.opBoolean","INTERSECT",EDGE,{"derivedFrom":[makeQuery(id+"F1.opRevolve","SWEPT_FACE",FACE,{"disambiguationData":[OSD([sQuery(id+"F0.wireOp",EDGE,"E4")])]}),makeQuery(id+"Fd9uYAkPvKm23FF_1.3.F5.opExtrude","SWEPT_FACE",FACE,{"disambiguationData":[OSD([sQuery(id+"F4.wireOp",EDGE,"E6.left")])]})]});
            var Q61;
            Q61=makeQuery(id+"Fd9uYAkPvKm23FF_1.4.F5.boolean.opBoolean","INTERSECT",EDGE,{"derivedFrom":[makeQuery(id+"F2.opShell","OFFSET_FACE",FACE,{"disambiguationData":[OSD([sQuery(id+"F0.wireOp",EDGE,"E4")])]}),makeQuery(id+"Fd9uYAkPvKm23FF_1.4.F5.opExtrude","SWEPT_FACE",FACE,{"disambiguationData":[OSD([sQuery(id+"F4.wireOp",EDGE,"E6.left")])]})]});
            var Q62;
            Q62=makeQuery(id+"Fd9uYAkPvKm23FF_1.4.F5.boolean.opBoolean","INTERSECT",EDGE,{"derivedFrom":[makeQuery(id+"F1.opRevolve","SWEPT_FACE",FACE,{"disambiguationData":[OSD([sQuery(id+"F0.wireOp",EDGE,"E4")])]}),makeQuery(id+"Fd9uYAkPvKm23FF_1.4.F5.opExtrude","SWEPT_FACE",FACE,{"disambiguationData":[OSD([sQuery(id+"F4.wireOp",EDGE,"E6.right")])]})]});
            var Q63;
            Q63=makeQuery(id+"Fd9uYAkPvKm23FF_1.4.F5.boolean.opBoolean","COPY",FACE,{"derivedFrom":makeQuery(id+"Fd9uYAkPvKm23FF_1.4.F5.opExtrude","SWEPT_FACE",FACE,{"disambiguationData":[OSD([sQuery(id+"F4.wireOp",EDGE,"E6.bottom")])]})});
            var Q64;
            Q64=makeQuery(id+"Fd9uYAkPvKm23FF_1.4.F5.boolean.opBoolean","COPY",FACE,{"derivedFrom":makeQuery(id+"Fd9uYAkPvKm23FF_1.4.F5.opExtrude","SWEPT_FACE",FACE,{"disambiguationData":[OSD([sQuery(id+"F4.wireOp",EDGE,"E6.top")])]})});
            var Q65;
            Q65=makeQuery(id+"Fd9uYAkPvKm23FF_1.4.F5.boolean.opBoolean","COPY",FACE,{"derivedFrom":makeQuery(id+"Fd9uYAkPvKm23FF_1.4.F5.opExtrude","SWEPT_FACE",FACE,{"disambiguationData":[OSD([sQuery(id+"F4.wireOp",EDGE,"E6.left")])]})});
            var Q66;
            Q66=makeQuery(id+"Fd9uYAkPvKm23FF_1.4.F5.boolean.opBoolean","COPY",FACE,{"derivedFrom":makeQuery(id+"Fd9uYAkPvKm23FF_1.4.F5.opExtrude","SWEPT_FACE",FACE,{"disambiguationData":[OSD([sQuery(id+"F4.wireOp",EDGE,"E6.right")])]})});
            var Q67;
            Q67=makeQuery(id+"Fd9uYAkPvKm23FF_1.4.F5.boolean.opBoolean","COPY",FACE,{"derivedFrom":makeQuery(id+"Fd9uYAkPvKm23FF_1.4.F5.opExtrude","SWEPT_FACE",FACE,{"disambiguationData":[OSD([sQuery(id+"F4.wireOp",EDGE,"E8.filletArc")])]})});
            var Q68;
            Q68=makeQuery(id+"Fd9uYAkPvKm23FF_1.4.F5.boolean.opBoolean","COPY",FACE,{"derivedFrom":makeQuery(id+"Fd9uYAkPvKm23FF_1.4.F5.opExtrude","SWEPT_FACE",FACE,{"disambiguationData":[OSD([sQuery(id+"F4.wireOp",EDGE,"E10.filletArc")])]})});
            var Q69;
            Q69=makeQuery(id+"Fd9uYAkPvKm23FF_1.4.F5.boolean.opBoolean","INTERSECT",EDGE,{"derivedFrom":[makeQuery(id+"F1.opRevolve","SWEPT_FACE",FACE,{"disambiguationData":[OSD([sQuery(id+"F0.wireOp",EDGE,"E4")])]}),makeQuery(id+"Fd9uYAkPvKm23FF_1.4.F5.opExtrude","SWEPT_FACE",FACE,{"disambiguationData":[OSD([sQuery(id+"F4.wireOp",EDGE,"E6.bottom")])]})]});
            var Q70;
            Q70=makeQuery(id+"Fd9uYAkPvKm23FF_1.4.F5.boolean.opBoolean","INTERSECT",EDGE,{"derivedFrom":[makeQuery(id+"F2.opShell","OFFSET_FACE",FACE,{"disambiguationData":[OSD([sQuery(id+"F0.wireOp",EDGE,"E4")])]}),makeQuery(id+"Fd9uYAkPvKm23FF_1.4.F5.opExtrude","SWEPT_FACE",FACE,{"disambiguationData":[OSD([sQuery(id+"F4.wireOp",EDGE,"E6.bottom")])]})]});
            var Q71;
            Q71=makeQuery(id+"Fd9uYAkPvKm23FF_1.4.F5.boolean.opBoolean","INTERSECT",EDGE,{"derivedFrom":[makeQuery(id+"F1.opRevolve","SWEPT_FACE",FACE,{"disambiguationData":[OSD([sQuery(id+"F0.wireOp",EDGE,"E4")])]}),makeQuery(id+"Fd9uYAkPvKm23FF_1.4.F5.opExtrude","SWEPT_FACE",FACE,{"disambiguationData":[OSD([sQuery(id+"F4.wireOp",EDGE,"E6.top")])]})]});
            var Q72;
            Q72=makeQuery(id+"Fd9uYAkPvKm23FF_1.4.F5.boolean.opBoolean","INTERSECT",EDGE,{"derivedFrom":[makeQuery(id+"F1.opRevolve","SWEPT_FACE",FACE,{"disambiguationData":[OSD([sQuery(id+"F0.wireOp",EDGE,"E4")])]}),makeQuery(id+"Fd9uYAkPvKm23FF_1.4.F5.opExtrude","SWEPT_FACE",FACE,{"disambiguationData":[OSD([sQuery(id+"F4.wireOp",EDGE,"E6.left")])]})]});
            var Q73;
            Q73=makeQuery(id+"Fd9uYAkPvKm23FF_1.5.F5.boolean.opBoolean","COPY",FACE,{"derivedFrom":makeQuery(id+"Fd9uYAkPvKm23FF_1.5.F5.opExtrude","SWEPT_FACE",FACE,{"disambiguationData":[OSD([sQuery(id+"F4.wireOp",EDGE,"E6.bottom")])]})});
            var Q74;
            Q74=makeQuery(id+"Fd9uYAkPvKm23FF_1.6.F5.boolean.opBoolean","INTERSECT",EDGE,{"derivedFrom":[makeQuery(id+"F2.opShell","OFFSET_FACE",FACE,{"disambiguationData":[OSD([sQuery(id+"F0.wireOp",EDGE,"E4")])]}),makeQuery(id+"Fd9uYAkPvKm23FF_1.6.F5.opExtrude","SWEPT_FACE",FACE,{"disambiguationData":[OSD([sQuery(id+"F4.wireOp",EDGE,"E6.left")])]})]});
            var Q75;
            Q75=makeQuery(id+"Fd9uYAkPvKm23FF_1.6.F5.boolean.opBoolean","INTERSECT",EDGE,{"derivedFrom":[makeQuery(id+"F2.opShell","OFFSET_FACE",FACE,{"disambiguationData":[OSD([sQuery(id+"F0.wireOp",EDGE,"E4")])]}),makeQuery(id+"Fd9uYAkPvKm23FF_1.6.F5.opExtrude","SWEPT_FACE",FACE,{"disambiguationData":[OSD([sQuery(id+"F4.wireOp",EDGE,"E6.right")])]})]});
            var Q76;
            Q76=makeQuery(id+"Fd9uYAkPvKm23FF_1.6.F5.boolean.opBoolean","COPY",FACE,{"derivedFrom":makeQuery(id+"Fd9uYAkPvKm23FF_1.6.F5.opExtrude","SWEPT_FACE",FACE,{"disambiguationData":[OSD([sQuery(id+"F4.wireOp",EDGE,"E6.bottom")])]})});
            var Q77;
            Q77=makeQuery(id+"Fd9uYAkPvKm23FF_1.6.F5.boolean.opBoolean","COPY",FACE,{"derivedFrom":makeQuery(id+"Fd9uYAkPvKm23FF_1.6.F5.opExtrude","SWEPT_FACE",FACE,{"disambiguationData":[OSD([sQuery(id+"F4.wireOp",EDGE,"E7.filletArc")])]})});
            var Q78;
            Q78=makeQuery(id+"Fd9uYAkPvKm23FF_1.6.F5.boolean.opBoolean","COPY",FACE,{"derivedFrom":makeQuery(id+"Fd9uYAkPvKm23FF_1.6.F5.opExtrude","SWEPT_FACE",FACE,{"disambiguationData":[OSD([sQuery(id+"F4.wireOp",EDGE,"E8.filletArc")])]})});
            var Q79;
            Q79=makeQuery(id+"Fd9uYAkPvKm23FF_1.6.F5.boolean.opBoolean","COPY",FACE,{"derivedFrom":makeQuery(id+"Fd9uYAkPvKm23FF_1.6.F5.opExtrude","SWEPT_FACE",FACE,{"disambiguationData":[OSD([sQuery(id+"F4.wireOp",EDGE,"E9.filletArc")])]})});
            var Q80;
            Q80=makeQuery(id+"Fd9uYAkPvKm23FF_1.6.F5.boolean.opBoolean","INTERSECT",EDGE,{"derivedFrom":[makeQuery(id+"F1.opRevolve","SWEPT_FACE",FACE,{"disambiguationData":[OSD([sQuery(id+"F0.wireOp",EDGE,"E4")])]}),makeQuery(id+"Fd9uYAkPvKm23FF_1.6.F5.opExtrude","SWEPT_FACE",FACE,{"disambiguationData":[OSD([sQuery(id+"F4.wireOp",EDGE,"E6.bottom")])]})]});
            var Q81;
            Q81=makeQuery(id+"F1.opRevolve","SWEPT_FACE",FACE,{"disambiguationData":[OSD([sQuery(id+"F0.wireOp",EDGE,"E4")])]});
            var Q82;
            Q82=makeQuery(id+"Fd9uYAkPvKm23FF_1.6.F5.boolean.opBoolean","INTERSECT",EDGE,{"derivedFrom":[makeQuery(id+"F2.opShell","OFFSET_FACE",FACE,{"disambiguationData":[OSD([sQuery(id+"F0.wireOp",EDGE,"E4")])]}),makeQuery(id+"Fd9uYAkPvKm23FF_1.6.F5.opExtrude","SWEPT_FACE",FACE,{"disambiguationData":[OSD([sQuery(id+"F4.wireOp",EDGE,"E6.bottom")])]})]});
            var Q83;
            Q83=makeQuery(id+"F2.opShell","OFFSET_FACE",FACE,{"disambiguationData":[OSD([sQuery(id+"F0.wireOp",EDGE,"E4")])]});
            var Q84;
            Q84=makeQuery(id+"Fd9uYAkPvKm23FF_1.6.F5.boolean.opBoolean","INTERSECT",EDGE,{"derivedFrom":[makeQuery(id+"F1.opRevolve","SWEPT_FACE",FACE,{"disambiguationData":[OSD([sQuery(id+"F0.wireOp",EDGE,"E4")])]}),makeQuery(id+"Fd9uYAkPvKm23FF_1.6.F5.opExtrude","SWEPT_FACE",FACE,{"disambiguationData":[OSD([sQuery(id+"F4.wireOp",EDGE,"E6.left")])]})]});
            var Q85;
            Q85=makeQuery(id+"Fd9uYAkPvKm23FF_1.1.F5.boolean.opBoolean","INTERSECT",EDGE,{"derivedFrom":[makeQuery(id+"F1.opRevolve","SWEPT_FACE",FACE,{"disambiguationData":[OSD([sQuery(id+"F0.wireOp",EDGE,"E4")])]}),makeQuery(id+"Fd9uYAkPvKm23FF_1.1.F5.opExtrude","SWEPT_FACE",FACE,{"disambiguationData":[OSD([sQuery(id+"F4.wireOp",EDGE,"E9.filletArc")])]})]});
            var Q86;
            Q86=makeQuery(id+"Fd9uYAkPvKm23FF_1.2.F5.boolean.opBoolean","INTERSECT",EDGE,{"derivedFrom":[makeQuery(id+"F1.opRevolve","SWEPT_FACE",FACE,{"disambiguationData":[OSD([sQuery(id+"F0.wireOp",EDGE,"E4")])]}),makeQuery(id+"Fd9uYAkPvKm23FF_1.2.F5.opExtrude","SWEPT_FACE",FACE,{"disambiguationData":[OSD([sQuery(id+"F4.wireOp",EDGE,"E8.filletArc")])]})]});
            var Q87;
            Q87=makeQuery(id+"Fd9uYAkPvKm23FF_1.3.F5.boolean.opBoolean","INTERSECT",EDGE,{"derivedFrom":[makeQuery(id+"F1.opRevolve","SWEPT_FACE",FACE,{"disambiguationData":[OSD([sQuery(id+"F0.wireOp",EDGE,"E4")])]}),makeQuery(id+"Fd9uYAkPvKm23FF_1.3.F5.opExtrude","SWEPT_FACE",FACE,{"disambiguationData":[OSD([sQuery(id+"F4.wireOp",EDGE,"E7.filletArc")])]})]});
            var Q88;
            Q88=makeQuery(id+"Fd9uYAkPvKm23FF_1.3.F5.boolean.opBoolean","INTERSECT",EDGE,{"derivedFrom":[makeQuery(id+"F1.opRevolve","SWEPT_FACE",FACE,{"disambiguationData":[OSD([sQuery(id+"F0.wireOp",EDGE,"E4")])]}),makeQuery(id+"Fd9uYAkPvKm23FF_1.3.F5.opExtrude","SWEPT_FACE",FACE,{"disambiguationData":[OSD([sQuery(id+"F4.wireOp",EDGE,"E10.filletArc")])]})]});
            var Q89;
            Q89=makeQuery(id+"Fd9uYAkPvKm23FF_1.6.F5.boolean.opBoolean","INTERSECT",EDGE,{"derivedFrom":[makeQuery(id+"F2.opShell","OFFSET_FACE",FACE,{"disambiguationData":[OSD([sQuery(id+"F0.wireOp",EDGE,"E4")])]}),makeQuery(id+"Fd9uYAkPvKm23FF_1.6.F5.opExtrude","SWEPT_FACE",FACE,{"disambiguationData":[OSD([sQuery(id+"F4.wireOp",EDGE,"E7.filletArc")])]})]});
            var Q90;
            Q90=makeQuery(id+"Fd9uYAkPvKm23FF_1.6.F5.boolean.opBoolean","INTERSECT",EDGE,{"derivedFrom":[makeQuery(id+"F2.opShell","OFFSET_FACE",FACE,{"disambiguationData":[OSD([sQuery(id+"F0.wireOp",EDGE,"E4")])]}),makeQuery(id+"Fd9uYAkPvKm23FF_1.6.F5.opExtrude","SWEPT_FACE",FACE,{"disambiguationData":[OSD([sQuery(id+"F4.wireOp",EDGE,"E8.filletArc")])]})]});
            var Q91;
            {var subQ0=sQuery(id+"F0.wireOp",EDGE,"E2");Q91=makeQuery(id+"F3.opFillet","BLEND_EDGE",EDGE,{"blendedFrom":[makeQuery(id+"F1.opRevolve","SWEPT_EDGE",EDGE,{"disambiguationData":[OSD([subQ0,sQuery(id+"F0.wireOp",EDGE,"E4")])]}),makeQuery(id+"F1.opRevolve","SWEPT_FACE",FACE,{"disambiguationData":[OSD([subQ0])]})],"blendedInto":[makeQuery(id+"F1.opRevolve","SWEPT_FACE",FACE,{"disambiguationData":[OSD([subQ0])]})]});}
            var Q92;
            {var subQ0=sQuery(id+"F0.wireOp",EDGE,"E2");Q92=makeQuery(id+"F3.opFillet","BLEND_EDGE",EDGE,{"blendedFrom":[makeQuery(id+"F1.opRevolve","SWEPT_EDGE",EDGE,{"disambiguationData":[OSD([sQuery(id+"F0.wireOp",EDGE,"E1"),subQ0])]}),makeQuery(id+"F1.opRevolve","SWEPT_FACE",FACE,{"disambiguationData":[OSD([subQ0])]})],"blendedInto":[makeQuery(id+"F1.opRevolve","SWEPT_FACE",FACE,{"disambiguationData":[OSD([subQ0])]})]});}
            var Q93;
            {var subQ0=sQuery(id+"F0.wireOp",EDGE,"E4");Q93=makeQuery(id+"F3.opFillet","BLEND_EDGE",EDGE,{"blendedFrom":[makeQuery(id+"F2.opShell","OFFSET_EDGE",EDGE,{"disambiguationData":[OSD([sQuery(id+"F0.wireOp",EDGE,"E3"),subQ0])]}),makeQuery(id+"F2.opShell","OFFSET_FACE",FACE,{"disambiguationData":[OSD([subQ0])]})],"blendedInto":[makeQuery(id+"F2.opShell","OFFSET_FACE",FACE,{"disambiguationData":[OSD([subQ0])]})]});}
            var Q94;
            {var subQ0=sQuery(id+"F0.wireOp",EDGE,"E3");Q94=makeQuery(id+"F3.opFillet","BLEND_EDGE",EDGE,{"blendedFrom":[makeQuery(id+"F2.opShell","OFFSET_EDGE",EDGE,{"disambiguationData":[OSD([subQ0,sQuery(id+"F0.wireOp",EDGE,"E4")])]}),makeQuery(id+"F2.opShell","OFFSET_FACE",FACE,{"disambiguationData":[OSD([subQ0])]})],"blendedInto":[makeQuery(id+"F2.opShell","OFFSET_FACE",FACE,{"disambiguationData":[OSD([subQ0])]})]});}
            var Q95;
            Q95=makeQuery(id+"F2.opShell","OFFSET_FACE",FACE,{"disambiguationData":[OSD([sQuery(id+"F0.wireOp",EDGE,"E3")])]});
            var Q96;
            Q96=makeQuery(id+"F5.boolean.opBoolean","COPY",EDGE,{"derivedFrom":makeQuery(id+"F5.opExtrude","SWEPT_EDGE",EDGE,{"disambiguationData":[OSD([sQuery(id+"F4.wireOp",EDGE,"E6.right"),sQuery(id+"F4.wireOp",EDGE,"E7.filletArc")])]})});
            var Q97;
            Q97=makeQuery(id+"F5.boolean.opBoolean","COPY",FACE,{"derivedFrom":makeQuery(id+"F5.opExtrude","SWEPT_FACE",FACE,{"disambiguationData":[OSD([sQuery(id+"F4.wireOp",EDGE,"E9.filletArc")])]})});
            var Q98;
            Q98=makeQuery(id+"F5.boolean.opBoolean","COPY",FACE,{"derivedFrom":makeQuery(id+"F5.opExtrude","SWEPT_FACE",FACE,{"disambiguationData":[OSD([sQuery(id+"F4.wireOp",EDGE,"E6.left")])]})});
            var Q99;
            {var subQ0=sQuery(id+"F0.wireOp",EDGE,"E4");var subQ1=sQuery(id+"F0.wireOp",EDGE,"E3");Q99=makeQuery(id+"F3.opFillet","BLEND_FACE",FACE,{"disambiguationData":[OSD([subQ1,subQ0]),TDD([makeQuery(id+"F2.opShell","OFFSET_EDGE",EDGE,{"disambiguationData":[OSD([subQ1,subQ0])]})])]});}
            var Q100;
            Q100=makeQuery(id+"F5.boolean.opBoolean","COPY",FACE,{"derivedFrom":makeQuery(id+"F5.opExtrude","SWEPT_FACE",FACE,{"disambiguationData":[OSD([sQuery(id+"F4.wireOp",EDGE,"E6.top")])]})});
            var Q101;
            Q101=makeQuery(id+"F5.boolean.opBoolean","COPY",EDGE,{"derivedFrom":makeQuery(id+"F5.opExtrude","SWEPT_EDGE",EDGE,{"disambiguationData":[OSD([sQuery(id+"F4.wireOp",EDGE,"E6.bottom"),sQuery(id+"F4.wireOp",EDGE,"E7.filletArc")])]})});
            var Q102;
            Q102=makeQuery(id+"F1.opRevolve","SWEPT_FACE",FACE,{"disambiguationData":[OSD([sQuery(id+"F0.wireOp",EDGE,"E2")])]});
            var Q103;
            {var subQ0=sQuery(id+"F0.wireOp",EDGE,"E3");Q103=makeQuery(id+"F3.opFillet","BLEND_EDGE",EDGE,{"blendedFrom":[makeQuery(id+"F2.opShell","OFFSET_EDGE",EDGE,{"disambiguationData":[OSD([sQuery(id+"F0.wireOp",EDGE,"E1"),subQ0])]}),makeQuery(id+"F2.opShell","OFFSET_FACE",FACE,{"disambiguationData":[OSD([subQ0])]})],"blendedInto":[makeQuery(id+"F2.opShell","OFFSET_FACE",FACE,{"disambiguationData":[OSD([subQ0])]})]});}
            var Q104;
            Q104=makeQuery(id+"F5.boolean.opBoolean","INTERSECT",EDGE,{"derivedFrom":[makeQuery(id+"F2.opShell","OFFSET_FACE",FACE,{"disambiguationData":[OSD([sQuery(id+"F0.wireOp",EDGE,"E4")])]}),makeQuery(id+"F5.opExtrude","SWEPT_FACE",FACE,{"disambiguationData":[OSD([sQuery(id+"F4.wireOp",EDGE,"E10.filletArc")])]})]});
            var Q105;
            Q105=makeQuery(id+"F5.boolean.opBoolean","INTERSECT",EDGE,{"derivedFrom":[makeQuery(id+"F1.opRevolve","SWEPT_FACE",FACE,{"disambiguationData":[OSD([sQuery(id+"F0.wireOp",EDGE,"E4")])]}),makeQuery(id+"F5.opExtrude","SWEPT_FACE",FACE,{"disambiguationData":[OSD([sQuery(id+"F4.wireOp",EDGE,"E9.filletArc")])]})]});
            var Q106;
            Q106=makeQuery(id+"F5.boolean.opBoolean","INTERSECT",EDGE,{"derivedFrom":[makeQuery(id+"F2.opShell","OFFSET_FACE",FACE,{"disambiguationData":[OSD([sQuery(id+"F0.wireOp",EDGE,"E4")])]}),makeQuery(id+"F5.opExtrude","SWEPT_FACE",FACE,{"disambiguationData":[OSD([sQuery(id+"F4.wireOp",EDGE,"E7.filletArc")])]})]});
            var Q107;
            Q107=makeQuery(id+"F5.boolean.opBoolean","INTERSECT",EDGE,{"derivedFrom":[makeQuery(id+"F1.opRevolve","SWEPT_FACE",FACE,{"disambiguationData":[OSD([sQuery(id+"F0.wireOp",EDGE,"E4")])]}),makeQuery(id+"F5.opExtrude","SWEPT_FACE",FACE,{"disambiguationData":[OSD([sQuery(id+"F4.wireOp",EDGE,"E7.filletArc")])]})]});
            var Q108;
            Q108=makeQuery(id+"F5.boolean.opBoolean","INTERSECT",EDGE,{"derivedFrom":[makeQuery(id+"F1.opRevolve","SWEPT_FACE",FACE,{"disambiguationData":[OSD([sQuery(id+"F0.wireOp",EDGE,"E4")])]}),makeQuery(id+"F5.opExtrude","SWEPT_FACE",FACE,{"disambiguationData":[OSD([sQuery(id+"F4.wireOp",EDGE,"E6.top")])]})]});
            var Q109;
            Q109=makeQuery(id+"Fd9uYAkPvKm23FF_1.3.F5.boolean.opBoolean","INTERSECT",EDGE,{"derivedFrom":[makeQuery(id+"F2.opShell","OFFSET_FACE",FACE,{"disambiguationData":[OSD([sQuery(id+"F0.wireOp",EDGE,"E4")])]}),makeQuery(id+"Fd9uYAkPvKm23FF_1.3.F5.opExtrude","SWEPT_FACE",FACE,{"disambiguationData":[OSD([sQuery(id+"F4.wireOp",EDGE,"E6.top")])]})]});
            var Q110;
            Q110=makeQuery(id+"Fd9uYAkPvKm23FF_1.3.F5.boolean.opBoolean","COPY",EDGE,{"derivedFrom":makeQuery(id+"Fd9uYAkPvKm23FF_1.3.F5.opExtrude","SWEPT_EDGE",EDGE,{"disambiguationData":[OSD([sQuery(id+"F4.wireOp",EDGE,"E6.right"),sQuery(id+"F4.wireOp",EDGE,"E10.filletArc")])]})});
            var Q111;
            Q111=makeQuery(id+"Fd9uYAkPvKm23FF_1.3.F5.boolean.opBoolean","COPY",EDGE,{"derivedFrom":makeQuery(id+"Fd9uYAkPvKm23FF_1.3.F5.opExtrude","SWEPT_EDGE",EDGE,{"disambiguationData":[OSD([sQuery(id+"F4.wireOp",EDGE,"E6.right"),sQuery(id+"F4.wireOp",EDGE,"E7.filletArc")])]})});
            var Q112;
            Q112=makeQuery(id+"Fd9uYAkPvKm23FF_1.3.F5.boolean.opBoolean","COPY",EDGE,{"derivedFrom":makeQuery(id+"Fd9uYAkPvKm23FF_1.3.F5.opExtrude","SWEPT_EDGE",EDGE,{"disambiguationData":[OSD([sQuery(id+"F4.wireOp",EDGE,"E6.left"),sQuery(id+"F4.wireOp",EDGE,"E9.filletArc")])]})});
            var Q113;
            Q113=makeQuery(id+"Fd9uYAkPvKm23FF_1.3.F5.boolean.opBoolean","COPY",EDGE,{"derivedFrom":makeQuery(id+"Fd9uYAkPvKm23FF_1.3.F5.opExtrude","SWEPT_EDGE",EDGE,{"disambiguationData":[OSD([sQuery(id+"F4.wireOp",EDGE,"E6.left"),sQuery(id+"F4.wireOp",EDGE,"E8.filletArc")])]})});
            var Q114;
            Q114=makeQuery(id+"Fd9uYAkPvKm23FF_1.3.F5.boolean.opBoolean","COPY",EDGE,{"derivedFrom":makeQuery(id+"Fd9uYAkPvKm23FF_1.3.F5.opExtrude","SWEPT_EDGE",EDGE,{"disambiguationData":[OSD([sQuery(id+"F4.wireOp",EDGE,"E6.top"),sQuery(id+"F4.wireOp",EDGE,"E10.filletArc")])]})});
            var Q115;
            Q115=makeQuery(id+"Fd9uYAkPvKm23FF_1.3.F5.boolean.opBoolean","COPY",EDGE,{"derivedFrom":makeQuery(id+"Fd9uYAkPvKm23FF_1.3.F5.opExtrude","SWEPT_EDGE",EDGE,{"disambiguationData":[OSD([sQuery(id+"F4.wireOp",EDGE,"E6.top"),sQuery(id+"F4.wireOp",EDGE,"E9.filletArc")])]})});
            var Q116;
            Q116=makeQuery(id+"Fd9uYAkPvKm23FF_1.3.F5.boolean.opBoolean","COPY",FACE,{"derivedFrom":makeQuery(id+"Fd9uYAkPvKm23FF_1.3.F5.opExtrude","SWEPT_FACE",FACE,{"disambiguationData":[OSD([sQuery(id+"F4.wireOp",EDGE,"E6.top")])]})});
            var Q117;
            Q117=makeQuery(id+"Fd9uYAkPvKm23FF_1.3.F5.boolean.opBoolean","COPY",EDGE,{"derivedFrom":makeQuery(id+"Fd9uYAkPvKm23FF_1.3.F5.opExtrude","SWEPT_EDGE",EDGE,{"disambiguationData":[OSD([sQuery(id+"F4.wireOp",EDGE,"E6.bottom"),sQuery(id+"F4.wireOp",EDGE,"E7.filletArc")])]})});
            var Q118;
            Q118=makeQuery(id+"Fd9uYAkPvKm23FF_1.3.F5.boolean.opBoolean","COPY",EDGE,{"derivedFrom":makeQuery(id+"Fd9uYAkPvKm23FF_1.3.F5.opExtrude","SWEPT_EDGE",EDGE,{"disambiguationData":[OSD([sQuery(id+"F4.wireOp",EDGE,"E6.bottom"),sQuery(id+"F4.wireOp",EDGE,"E8.filletArc")])]})});
            var Q119;
            Q119=makeQuery(id+"Fd9uYAkPvKm23FF_1.3.F5.boolean.opBoolean","INTERSECT",EDGE,{"derivedFrom":[makeQuery(id+"F2.opShell","OFFSET_FACE",FACE,{"disambiguationData":[OSD([sQuery(id+"F0.wireOp",EDGE,"E4")])]}),makeQuery(id+"Fd9uYAkPvKm23FF_1.3.F5.opExtrude","SWEPT_FACE",FACE,{"disambiguationData":[OSD([sQuery(id+"F4.wireOp",EDGE,"E6.right")])]})]});
            var Q120;
            Q120=makeQuery(id+"Fd9uYAkPvKm23FF_1.3.F5.boolean.opBoolean","INTERSECT",EDGE,{"derivedFrom":[makeQuery(id+"F2.opShell","OFFSET_FACE",FACE,{"disambiguationData":[OSD([sQuery(id+"F0.wireOp",EDGE,"E4")])]}),makeQuery(id+"Fd9uYAkPvKm23FF_1.3.F5.opExtrude","SWEPT_FACE",FACE,{"disambiguationData":[OSD([sQuery(id+"F4.wireOp",EDGE,"E6.left")])]})]});
            var Q121;
            Q121=makeQuery(id+"Fd9uYAkPvKm23FF_1.2.F5.boolean.opBoolean","INTERSECT",EDGE,{"derivedFrom":[makeQuery(id+"F2.opShell","OFFSET_FACE",FACE,{"disambiguationData":[OSD([sQuery(id+"F0.wireOp",EDGE,"E4")])]}),makeQuery(id+"Fd9uYAkPvKm23FF_1.2.F5.opExtrude","SWEPT_FACE",FACE,{"disambiguationData":[OSD([sQuery(id+"F4.wireOp",EDGE,"E6.top")])]})]});
            var Q122;
            Q122=makeQuery(id+"Fd9uYAkPvKm23FF_1.2.F5.boolean.opBoolean","COPY",FACE,{"derivedFrom":makeQuery(id+"Fd9uYAkPvKm23FF_1.2.F5.opExtrude","SWEPT_FACE",FACE,{"disambiguationData":[OSD([sQuery(id+"F4.wireOp",EDGE,"E10.filletArc")])]})});
            var Q123;
            Q123=makeQuery(id+"Fd9uYAkPvKm23FF_1.2.F5.boolean.opBoolean","COPY",EDGE,{"derivedFrom":makeQuery(id+"Fd9uYAkPvKm23FF_1.2.F5.opExtrude","SWEPT_EDGE",EDGE,{"disambiguationData":[OSD([sQuery(id+"F4.wireOp",EDGE,"E6.right"),sQuery(id+"F4.wireOp",EDGE,"E7.filletArc")])]})});
            var Q124;
            Q124=makeQuery(id+"Fd9uYAkPvKm23FF_1.2.F5.boolean.opBoolean","COPY",FACE,{"derivedFrom":makeQuery(id+"Fd9uYAkPvKm23FF_1.2.F5.opExtrude","SWEPT_FACE",FACE,{"disambiguationData":[OSD([sQuery(id+"F4.wireOp",EDGE,"E7.filletArc")])]})});
            var Q125;
            Q125=makeQuery(id+"Fd9uYAkPvKm23FF_1.2.F5.boolean.opBoolean","COPY",EDGE,{"derivedFrom":makeQuery(id+"Fd9uYAkPvKm23FF_1.2.F5.opExtrude","SWEPT_EDGE",EDGE,{"disambiguationData":[OSD([sQuery(id+"F4.wireOp",EDGE,"E6.left"),sQuery(id+"F4.wireOp",EDGE,"E8.filletArc")])]})});
            var Q126;
            Q126=makeQuery(id+"Fd9uYAkPvKm23FF_1.2.F5.boolean.opBoolean","COPY",EDGE,{"derivedFrom":makeQuery(id+"Fd9uYAkPvKm23FF_1.2.F5.opExtrude","SWEPT_EDGE",EDGE,{"disambiguationData":[OSD([sQuery(id+"F4.wireOp",EDGE,"E6.top"),sQuery(id+"F4.wireOp",EDGE,"E10.filletArc")])]})});
            var Q127;
            Q127=makeQuery(id+"Fd9uYAkPvKm23FF_1.2.F5.boolean.opBoolean","COPY",FACE,{"derivedFrom":makeQuery(id+"Fd9uYAkPvKm23FF_1.2.F5.opExtrude","SWEPT_FACE",FACE,{"disambiguationData":[OSD([sQuery(id+"F4.wireOp",EDGE,"E6.left")])]})});
            var Q128;
            Q128=makeQuery(id+"Fd9uYAkPvKm23FF_1.2.F5.boolean.opBoolean","COPY",EDGE,{"derivedFrom":makeQuery(id+"Fd9uYAkPvKm23FF_1.2.F5.opExtrude","SWEPT_EDGE",EDGE,{"disambiguationData":[OSD([sQuery(id+"F4.wireOp",EDGE,"E6.top"),sQuery(id+"F4.wireOp",EDGE,"E9.filletArc")])]})});
            var Q129;
            Q129=makeQuery(id+"Fd9uYAkPvKm23FF_1.2.F5.boolean.opBoolean","COPY",EDGE,{"derivedFrom":makeQuery(id+"Fd9uYAkPvKm23FF_1.2.F5.opExtrude","SWEPT_EDGE",EDGE,{"disambiguationData":[OSD([sQuery(id+"F4.wireOp",EDGE,"E6.bottom"),sQuery(id+"F4.wireOp",EDGE,"E7.filletArc")])]})});
            var Q130;
            Q130=makeQuery(id+"Fd9uYAkPvKm23FF_1.2.F5.boolean.opBoolean","COPY",EDGE,{"derivedFrom":makeQuery(id+"Fd9uYAkPvKm23FF_1.2.F5.opExtrude","SWEPT_EDGE",EDGE,{"disambiguationData":[OSD([sQuery(id+"F4.wireOp",EDGE,"E6.bottom"),sQuery(id+"F4.wireOp",EDGE,"E8.filletArc")])]})});
            var Q131;
            Q131=makeQuery(id+"Fd9uYAkPvKm23FF_1.2.F5.boolean.opBoolean","INTERSECT",EDGE,{"derivedFrom":[makeQuery(id+"F2.opShell","OFFSET_FACE",FACE,{"disambiguationData":[OSD([sQuery(id+"F0.wireOp",EDGE,"E4")])]}),makeQuery(id+"Fd9uYAkPvKm23FF_1.2.F5.opExtrude","SWEPT_FACE",FACE,{"disambiguationData":[OSD([sQuery(id+"F4.wireOp",EDGE,"E6.left")])]})]});
            var Q132;
            Q132=makeQuery(id+"Fd9uYAkPvKm23FF_1.1.F5.boolean.opBoolean","INTERSECT",EDGE,{"derivedFrom":[makeQuery(id+"F2.opShell","OFFSET_FACE",FACE,{"disambiguationData":[OSD([sQuery(id+"F0.wireOp",EDGE,"E4")])]}),makeQuery(id+"Fd9uYAkPvKm23FF_1.1.F5.opExtrude","SWEPT_FACE",FACE,{"disambiguationData":[OSD([sQuery(id+"F4.wireOp",EDGE,"E6.top")])]})]});
            var Q133;
            Q133=makeQuery(id+"Fd9uYAkPvKm23FF_1.1.F5.boolean.opBoolean","COPY",FACE,{"derivedFrom":makeQuery(id+"Fd9uYAkPvKm23FF_1.1.F5.opExtrude","SWEPT_FACE",FACE,{"disambiguationData":[OSD([sQuery(id+"F4.wireOp",EDGE,"E10.filletArc")])]})});
            var Q134;
            Q134=makeQuery(id+"Fd9uYAkPvKm23FF_1.1.F5.boolean.opBoolean","COPY",FACE,{"derivedFrom":makeQuery(id+"Fd9uYAkPvKm23FF_1.1.F5.opExtrude","SWEPT_FACE",FACE,{"disambiguationData":[OSD([sQuery(id+"F4.wireOp",EDGE,"E9.filletArc")])]})});
            var Q135;
            Q135=makeQuery(id+"Fd9uYAkPvKm23FF_1.1.F5.boolean.opBoolean","COPY",EDGE,{"derivedFrom":makeQuery(id+"Fd9uYAkPvKm23FF_1.1.F5.opExtrude","SWEPT_EDGE",EDGE,{"disambiguationData":[OSD([sQuery(id+"F4.wireOp",EDGE,"E6.right"),sQuery(id+"F4.wireOp",EDGE,"E7.filletArc")])]})});
            var Q136;
            Q136=makeQuery(id+"Fd9uYAkPvKm23FF_1.1.F5.boolean.opBoolean","COPY",FACE,{"derivedFrom":makeQuery(id+"Fd9uYAkPvKm23FF_1.1.F5.opExtrude","SWEPT_FACE",FACE,{"disambiguationData":[OSD([sQuery(id+"F4.wireOp",EDGE,"E8.filletArc")])]})});
            var Q137;
            Q137=makeQuery(id+"Fd9uYAkPvKm23FF_1.1.F5.boolean.opBoolean","COPY",EDGE,{"derivedFrom":makeQuery(id+"Fd9uYAkPvKm23FF_1.1.F5.opExtrude","SWEPT_EDGE",EDGE,{"disambiguationData":[OSD([sQuery(id+"F4.wireOp",EDGE,"E6.left"),sQuery(id+"F4.wireOp",EDGE,"E8.filletArc")])]})});
            var Q138;
            Q138=makeQuery(id+"Fd9uYAkPvKm23FF_1.1.F5.boolean.opBoolean","COPY",EDGE,{"derivedFrom":makeQuery(id+"Fd9uYAkPvKm23FF_1.1.F5.opExtrude","SWEPT_EDGE",EDGE,{"disambiguationData":[OSD([sQuery(id+"F4.wireOp",EDGE,"E6.top"),sQuery(id+"F4.wireOp",EDGE,"E10.filletArc")])]})});
            var Q139;
            Q139=makeQuery(id+"Fd9uYAkPvKm23FF_1.1.F5.boolean.opBoolean","COPY",FACE,{"derivedFrom":makeQuery(id+"Fd9uYAkPvKm23FF_1.1.F5.opExtrude","SWEPT_FACE",FACE,{"disambiguationData":[OSD([sQuery(id+"F4.wireOp",EDGE,"E6.left")])]})});
            var Q140;
            Q140=makeQuery(id+"Fd9uYAkPvKm23FF_1.1.F5.boolean.opBoolean","COPY",EDGE,{"derivedFrom":makeQuery(id+"Fd9uYAkPvKm23FF_1.1.F5.opExtrude","SWEPT_EDGE",EDGE,{"disambiguationData":[OSD([sQuery(id+"F4.wireOp",EDGE,"E6.bottom"),sQuery(id+"F4.wireOp",EDGE,"E7.filletArc")])]})});
            var Q141;
            Q141=makeQuery(id+"Fd9uYAkPvKm23FF_1.1.F5.boolean.opBoolean","COPY",EDGE,{"derivedFrom":makeQuery(id+"Fd9uYAkPvKm23FF_1.1.F5.opExtrude","SWEPT_EDGE",EDGE,{"disambiguationData":[OSD([sQuery(id+"F4.wireOp",EDGE,"E6.bottom"),sQuery(id+"F4.wireOp",EDGE,"E8.filletArc")])]})});
            var Q142;
            Q142=makeQuery(id+"Fd9uYAkPvKm23FF_1.1.F5.boolean.opBoolean","INTERSECT",EDGE,{"derivedFrom":[makeQuery(id+"F2.opShell","OFFSET_FACE",FACE,{"disambiguationData":[OSD([sQuery(id+"F0.wireOp",EDGE,"E4")])]}),makeQuery(id+"Fd9uYAkPvKm23FF_1.1.F5.opExtrude","SWEPT_FACE",FACE,{"disambiguationData":[OSD([sQuery(id+"F4.wireOp",EDGE,"E6.right")])]})]});
            var Q143;
            Q143=makeQuery(id+"Fd9uYAkPvKm23FF_1.1.F5.boolean.opBoolean","INTERSECT",EDGE,{"derivedFrom":[makeQuery(id+"F2.opShell","OFFSET_FACE",FACE,{"disambiguationData":[OSD([sQuery(id+"F0.wireOp",EDGE,"E4")])]}),makeQuery(id+"Fd9uYAkPvKm23FF_1.1.F5.opExtrude","SWEPT_FACE",FACE,{"disambiguationData":[OSD([sQuery(id+"F4.wireOp",EDGE,"E6.left")])]})]});
            var Q144;
            Q144=makeQuery(id+"Fd9uYAkPvKm23FF_1.4.F5.boolean.opBoolean","INTERSECT",EDGE,{"derivedFrom":[makeQuery(id+"F2.opShell","OFFSET_FACE",FACE,{"disambiguationData":[OSD([sQuery(id+"F0.wireOp",EDGE,"E4")])]}),makeQuery(id+"Fd9uYAkPvKm23FF_1.4.F5.opExtrude","SWEPT_FACE",FACE,{"disambiguationData":[OSD([sQuery(id+"F4.wireOp",EDGE,"E6.right")])]})]});
            var Q145;
            Q145=makeQuery(id+"Fd9uYAkPvKm23FF_1.4.F5.boolean.opBoolean","COPY",EDGE,{"derivedFrom":makeQuery(id+"Fd9uYAkPvKm23FF_1.4.F5.opExtrude","SWEPT_EDGE",EDGE,{"disambiguationData":[OSD([sQuery(id+"F4.wireOp",EDGE,"E6.bottom"),sQuery(id+"F4.wireOp",EDGE,"E8.filletArc")])]})});
            var Q146;
            Q146=makeQuery(id+"Fd9uYAkPvKm23FF_1.4.F5.boolean.opBoolean","COPY",EDGE,{"derivedFrom":makeQuery(id+"Fd9uYAkPvKm23FF_1.4.F5.opExtrude","SWEPT_EDGE",EDGE,{"disambiguationData":[OSD([sQuery(id+"F4.wireOp",EDGE,"E6.bottom"),sQuery(id+"F4.wireOp",EDGE,"E7.filletArc")])]})});
            var Q147;
            Q147=makeQuery(id+"Fd9uYAkPvKm23FF_1.4.F5.boolean.opBoolean","COPY",EDGE,{"derivedFrom":makeQuery(id+"Fd9uYAkPvKm23FF_1.4.F5.opExtrude","SWEPT_EDGE",EDGE,{"disambiguationData":[OSD([sQuery(id+"F4.wireOp",EDGE,"E6.top"),sQuery(id+"F4.wireOp",EDGE,"E9.filletArc")])]})});
            var Q148;
            Q148=makeQuery(id+"Fd9uYAkPvKm23FF_1.4.F5.boolean.opBoolean","COPY",EDGE,{"derivedFrom":makeQuery(id+"Fd9uYAkPvKm23FF_1.4.F5.opExtrude","SWEPT_EDGE",EDGE,{"disambiguationData":[OSD([sQuery(id+"F4.wireOp",EDGE,"E6.top"),sQuery(id+"F4.wireOp",EDGE,"E10.filletArc")])]})});
            var Q149;
            Q149=makeQuery(id+"Fd9uYAkPvKm23FF_1.4.F5.boolean.opBoolean","COPY",EDGE,{"derivedFrom":makeQuery(id+"Fd9uYAkPvKm23FF_1.4.F5.opExtrude","SWEPT_EDGE",EDGE,{"disambiguationData":[OSD([sQuery(id+"F4.wireOp",EDGE,"E6.left"),sQuery(id+"F4.wireOp",EDGE,"E8.filletArc")])]})});
            var Q150;
            Q150=makeQuery(id+"Fd9uYAkPvKm23FF_1.4.F5.boolean.opBoolean","COPY",FACE,{"derivedFrom":makeQuery(id+"Fd9uYAkPvKm23FF_1.4.F5.opExtrude","SWEPT_FACE",FACE,{"disambiguationData":[OSD([sQuery(id+"F4.wireOp",EDGE,"E7.filletArc")])]})});
            var Q151;
            Q151=makeQuery(id+"Fd9uYAkPvKm23FF_1.4.F5.boolean.opBoolean","COPY",EDGE,{"derivedFrom":makeQuery(id+"Fd9uYAkPvKm23FF_1.4.F5.opExtrude","SWEPT_EDGE",EDGE,{"disambiguationData":[OSD([sQuery(id+"F4.wireOp",EDGE,"E6.left"),sQuery(id+"F4.wireOp",EDGE,"E9.filletArc")])]})});
            var Q152;
            Q152=makeQuery(id+"Fd9uYAkPvKm23FF_1.4.F5.boolean.opBoolean","COPY",EDGE,{"derivedFrom":makeQuery(id+"Fd9uYAkPvKm23FF_1.4.F5.opExtrude","SWEPT_EDGE",EDGE,{"disambiguationData":[OSD([sQuery(id+"F4.wireOp",EDGE,"E6.right"),sQuery(id+"F4.wireOp",EDGE,"E7.filletArc")])]})});
            var Q153;
            Q153=makeQuery(id+"Fd9uYAkPvKm23FF_1.4.F5.boolean.opBoolean","COPY",FACE,{"derivedFrom":makeQuery(id+"Fd9uYAkPvKm23FF_1.4.F5.opExtrude","SWEPT_FACE",FACE,{"disambiguationData":[OSD([sQuery(id+"F4.wireOp",EDGE,"E9.filletArc")])]})});
            var Q154;
            Q154=makeQuery(id+"Fd9uYAkPvKm23FF_1.4.F5.boolean.opBoolean","COPY",EDGE,{"derivedFrom":makeQuery(id+"Fd9uYAkPvKm23FF_1.4.F5.opExtrude","SWEPT_EDGE",EDGE,{"disambiguationData":[OSD([sQuery(id+"F4.wireOp",EDGE,"E6.right"),sQuery(id+"F4.wireOp",EDGE,"E10.filletArc")])]})});
            var Q155;
            Q155=makeQuery(id+"Fd9uYAkPvKm23FF_1.4.F5.boolean.opBoolean","INTERSECT",EDGE,{"derivedFrom":[makeQuery(id+"F2.opShell","OFFSET_FACE",FACE,{"disambiguationData":[OSD([sQuery(id+"F0.wireOp",EDGE,"E4")])]}),makeQuery(id+"Fd9uYAkPvKm23FF_1.4.F5.opExtrude","SWEPT_FACE",FACE,{"disambiguationData":[OSD([sQuery(id+"F4.wireOp",EDGE,"E6.top")])]})]});
            var Q156;
            Q156=makeQuery(id+"Fd9uYAkPvKm23FF_1.5.F5.boolean.opBoolean","INTERSECT",EDGE,{"derivedFrom":[makeQuery(id+"F2.opShell","OFFSET_FACE",FACE,{"disambiguationData":[OSD([sQuery(id+"F0.wireOp",EDGE,"E4")])]}),makeQuery(id+"Fd9uYAkPvKm23FF_1.5.F5.opExtrude","SWEPT_FACE",FACE,{"disambiguationData":[OSD([sQuery(id+"F4.wireOp",EDGE,"E6.left")])]})]});
            var Q157;
            Q157=makeQuery(id+"Fd9uYAkPvKm23FF_1.5.F5.boolean.opBoolean","INTERSECT",EDGE,{"derivedFrom":[makeQuery(id+"F1.opRevolve","SWEPT_FACE",FACE,{"disambiguationData":[OSD([sQuery(id+"F0.wireOp",EDGE,"E4")])]}),makeQuery(id+"Fd9uYAkPvKm23FF_1.5.F5.opExtrude","SWEPT_FACE",FACE,{"disambiguationData":[OSD([sQuery(id+"F4.wireOp",EDGE,"E6.right")])]})]});
            var Q158;
            Q158=makeQuery(id+"Fd9uYAkPvKm23FF_1.5.F5.boolean.opBoolean","INTERSECT",EDGE,{"derivedFrom":[makeQuery(id+"F2.opShell","OFFSET_FACE",FACE,{"disambiguationData":[OSD([sQuery(id+"F0.wireOp",EDGE,"E4")])]}),makeQuery(id+"Fd9uYAkPvKm23FF_1.5.F5.opExtrude","SWEPT_FACE",FACE,{"disambiguationData":[OSD([sQuery(id+"F4.wireOp",EDGE,"E6.right")])]})]});
            var Q159;
            Q159=makeQuery(id+"Fd9uYAkPvKm23FF_1.5.F5.boolean.opBoolean","COPY",FACE,{"derivedFrom":makeQuery(id+"Fd9uYAkPvKm23FF_1.5.F5.opExtrude","SWEPT_FACE",FACE,{"disambiguationData":[OSD([sQuery(id+"F4.wireOp",EDGE,"E6.top")])]})});
            var Q160;
            Q160=makeQuery(id+"Fd9uYAkPvKm23FF_1.5.F5.boolean.opBoolean","COPY",FACE,{"derivedFrom":makeQuery(id+"Fd9uYAkPvKm23FF_1.5.F5.opExtrude","SWEPT_FACE",FACE,{"disambiguationData":[OSD([sQuery(id+"F4.wireOp",EDGE,"E6.left")])]})});
            var Q161;
            Q161=makeQuery(id+"Fd9uYAkPvKm23FF_1.5.F5.boolean.opBoolean","COPY",FACE,{"derivedFrom":makeQuery(id+"Fd9uYAkPvKm23FF_1.5.F5.opExtrude","SWEPT_FACE",FACE,{"disambiguationData":[OSD([sQuery(id+"F4.wireOp",EDGE,"E6.right")])]})});
            var Q162;
            Q162=makeQuery(id+"Fd9uYAkPvKm23FF_1.5.F5.boolean.opBoolean","COPY",FACE,{"derivedFrom":makeQuery(id+"Fd9uYAkPvKm23FF_1.5.F5.opExtrude","SWEPT_FACE",FACE,{"disambiguationData":[OSD([sQuery(id+"F4.wireOp",EDGE,"E7.filletArc")])]})});
            var Q163;
            Q163=makeQuery(id+"Fd9uYAkPvKm23FF_1.5.F5.boolean.opBoolean","COPY",FACE,{"derivedFrom":makeQuery(id+"Fd9uYAkPvKm23FF_1.5.F5.opExtrude","SWEPT_FACE",FACE,{"disambiguationData":[OSD([sQuery(id+"F4.wireOp",EDGE,"E8.filletArc")])]})});
            var Q164;
            Q164=makeQuery(id+"Fd9uYAkPvKm23FF_1.5.F5.boolean.opBoolean","COPY",FACE,{"derivedFrom":makeQuery(id+"Fd9uYAkPvKm23FF_1.5.F5.opExtrude","SWEPT_FACE",FACE,{"disambiguationData":[OSD([sQuery(id+"F4.wireOp",EDGE,"E10.filletArc")])]})});
            var Q165;
            Q165=makeQuery(id+"Fd9uYAkPvKm23FF_1.5.F5.boolean.opBoolean","INTERSECT",EDGE,{"derivedFrom":[makeQuery(id+"F1.opRevolve","SWEPT_FACE",FACE,{"disambiguationData":[OSD([sQuery(id+"F0.wireOp",EDGE,"E4")])]}),makeQuery(id+"Fd9uYAkPvKm23FF_1.5.F5.opExtrude","SWEPT_FACE",FACE,{"disambiguationData":[OSD([sQuery(id+"F4.wireOp",EDGE,"E6.bottom")])]})]});
            var Q166;
            Q166=makeQuery(id+"Fd9uYAkPvKm23FF_1.5.F5.boolean.opBoolean","INTERSECT",EDGE,{"derivedFrom":[makeQuery(id+"F2.opShell","OFFSET_FACE",FACE,{"disambiguationData":[OSD([sQuery(id+"F0.wireOp",EDGE,"E4")])]}),makeQuery(id+"Fd9uYAkPvKm23FF_1.5.F5.opExtrude","SWEPT_FACE",FACE,{"disambiguationData":[OSD([sQuery(id+"F4.wireOp",EDGE,"E6.bottom")])]})]});
            var Q167;
            Q167=makeQuery(id+"Fd9uYAkPvKm23FF_1.5.F5.boolean.opBoolean","INTERSECT",EDGE,{"derivedFrom":[makeQuery(id+"F1.opRevolve","SWEPT_FACE",FACE,{"disambiguationData":[OSD([sQuery(id+"F0.wireOp",EDGE,"E4")])]}),makeQuery(id+"Fd9uYAkPvKm23FF_1.5.F5.opExtrude","SWEPT_FACE",FACE,{"disambiguationData":[OSD([sQuery(id+"F4.wireOp",EDGE,"E6.top")])]})]});
            var Q168;
            Q168=makeQuery(id+"Fd9uYAkPvKm23FF_1.5.F5.boolean.opBoolean","INTERSECT",EDGE,{"derivedFrom":[makeQuery(id+"F1.opRevolve","SWEPT_FACE",FACE,{"disambiguationData":[OSD([sQuery(id+"F0.wireOp",EDGE,"E4")])]}),makeQuery(id+"Fd9uYAkPvKm23FF_1.5.F5.opExtrude","SWEPT_FACE",FACE,{"disambiguationData":[OSD([sQuery(id+"F4.wireOp",EDGE,"E6.left")])]})]});
            var Q169;
            Q169=makeQuery(id+"Fd9uYAkPvKm23FF_1.6.F5.boolean.opBoolean","INTERSECT",EDGE,{"derivedFrom":[makeQuery(id+"F1.opRevolve","SWEPT_FACE",FACE,{"disambiguationData":[OSD([sQuery(id+"F0.wireOp",EDGE,"E4")])]}),makeQuery(id+"Fd9uYAkPvKm23FF_1.6.F5.opExtrude","SWEPT_FACE",FACE,{"disambiguationData":[OSD([sQuery(id+"F4.wireOp",EDGE,"E6.right")])]})]});
            var Q170;
            Q170=makeQuery(id+"Fd9uYAkPvKm23FF_1.6.F5.boolean.opBoolean","COPY",EDGE,{"derivedFrom":makeQuery(id+"Fd9uYAkPvKm23FF_1.6.F5.opExtrude","SWEPT_EDGE",EDGE,{"disambiguationData":[OSD([sQuery(id+"F4.wireOp",EDGE,"E6.bottom"),sQuery(id+"F4.wireOp",EDGE,"E8.filletArc")])]})});
            var Q171;
            Q171=makeQuery(id+"Fd9uYAkPvKm23FF_1.6.F5.boolean.opBoolean","COPY",EDGE,{"derivedFrom":makeQuery(id+"Fd9uYAkPvKm23FF_1.6.F5.opExtrude","SWEPT_EDGE",EDGE,{"disambiguationData":[OSD([sQuery(id+"F4.wireOp",EDGE,"E6.bottom"),sQuery(id+"F4.wireOp",EDGE,"E7.filletArc")])]})});
            var Q172;
            Q172=makeQuery(id+"Fd9uYAkPvKm23FF_1.6.F5.boolean.opBoolean","COPY",FACE,{"derivedFrom":makeQuery(id+"Fd9uYAkPvKm23FF_1.6.F5.opExtrude","SWEPT_FACE",FACE,{"disambiguationData":[OSD([sQuery(id+"F4.wireOp",EDGE,"E6.top")])]})});
            var Q173;
            Q173=makeQuery(id+"Fd9uYAkPvKm23FF_1.6.F5.boolean.opBoolean","COPY",FACE,{"derivedFrom":makeQuery(id+"Fd9uYAkPvKm23FF_1.6.F5.opExtrude","SWEPT_FACE",FACE,{"disambiguationData":[OSD([sQuery(id+"F4.wireOp",EDGE,"E6.left")])]})});
            var Q174;
            Q174=makeQuery(id+"Fd9uYAkPvKm23FF_1.6.F5.boolean.opBoolean","COPY",FACE,{"derivedFrom":makeQuery(id+"Fd9uYAkPvKm23FF_1.6.F5.opExtrude","SWEPT_FACE",FACE,{"disambiguationData":[OSD([sQuery(id+"F4.wireOp",EDGE,"E6.right")])]})});
            var Q175;
            Q175=makeQuery(id+"Fd9uYAkPvKm23FF_1.6.F5.boolean.opBoolean","COPY",EDGE,{"derivedFrom":makeQuery(id+"Fd9uYAkPvKm23FF_1.6.F5.opExtrude","SWEPT_EDGE",EDGE,{"disambiguationData":[OSD([sQuery(id+"F4.wireOp",EDGE,"E6.right"),sQuery(id+"F4.wireOp",EDGE,"E7.filletArc")])]})});
            var Q176;
            Q176=makeQuery(id+"Fd9uYAkPvKm23FF_1.6.F5.boolean.opBoolean","COPY",EDGE,{"derivedFrom":makeQuery(id+"Fd9uYAkPvKm23FF_1.6.F5.opExtrude","SWEPT_EDGE",EDGE,{"disambiguationData":[OSD([sQuery(id+"F4.wireOp",EDGE,"E6.right"),sQuery(id+"F4.wireOp",EDGE,"E10.filletArc")])]})});
            var Q177;
            Q177=makeQuery(id+"Fd9uYAkPvKm23FF_1.6.F5.boolean.opBoolean","COPY",FACE,{"derivedFrom":makeQuery(id+"Fd9uYAkPvKm23FF_1.6.F5.opExtrude","SWEPT_FACE",FACE,{"disambiguationData":[OSD([sQuery(id+"F4.wireOp",EDGE,"E10.filletArc")])]})});
            var Q178;
            Q178=makeQuery(id+"Fd9uYAkPvKm23FF_1.6.F5.boolean.opBoolean","INTERSECT",EDGE,{"derivedFrom":[makeQuery(id+"F1.opRevolve","SWEPT_FACE",FACE,{"disambiguationData":[OSD([sQuery(id+"F0.wireOp",EDGE,"E4")])]}),makeQuery(id+"Fd9uYAkPvKm23FF_1.6.F5.opExtrude","SWEPT_FACE",FACE,{"disambiguationData":[OSD([sQuery(id+"F4.wireOp",EDGE,"E6.top")])]})]});
            var Q179;
            Q179=makeQuery(id+"Fd9uYAkPvKm23FF_1.1.F5.boolean.opBoolean","INTERSECT",EDGE,{"derivedFrom":[makeQuery(id+"F1.opRevolve","SWEPT_FACE",FACE,{"disambiguationData":[OSD([sQuery(id+"F0.wireOp",EDGE,"E4")])]}),makeQuery(id+"Fd9uYAkPvKm23FF_1.1.F5.opExtrude","SWEPT_FACE",FACE,{"disambiguationData":[OSD([sQuery(id+"F4.wireOp",EDGE,"E7.filletArc")])]})]});
            var Q180;
            Q180=makeQuery(id+"Fd9uYAkPvKm23FF_1.1.F5.boolean.opBoolean","INTERSECT",EDGE,{"derivedFrom":[makeQuery(id+"F1.opRevolve","SWEPT_FACE",FACE,{"disambiguationData":[OSD([sQuery(id+"F0.wireOp",EDGE,"E4")])]}),makeQuery(id+"Fd9uYAkPvKm23FF_1.1.F5.opExtrude","SWEPT_FACE",FACE,{"disambiguationData":[OSD([sQuery(id+"F4.wireOp",EDGE,"E8.filletArc")])]})]});
            var Q181;
            Q181=makeQuery(id+"Fd9uYAkPvKm23FF_1.1.F5.boolean.opBoolean","INTERSECT",EDGE,{"derivedFrom":[makeQuery(id+"F2.opShell","OFFSET_FACE",FACE,{"disambiguationData":[OSD([sQuery(id+"F0.wireOp",EDGE,"E4")])]}),makeQuery(id+"Fd9uYAkPvKm23FF_1.1.F5.opExtrude","SWEPT_FACE",FACE,{"disambiguationData":[OSD([sQuery(id+"F4.wireOp",EDGE,"E9.filletArc")])]})]});
            var Q182;
            Q182=makeQuery(id+"Fd9uYAkPvKm23FF_1.2.F5.boolean.opBoolean","INTERSECT",EDGE,{"derivedFrom":[makeQuery(id+"F1.opRevolve","SWEPT_FACE",FACE,{"disambiguationData":[OSD([sQuery(id+"F0.wireOp",EDGE,"E4")])]}),makeQuery(id+"Fd9uYAkPvKm23FF_1.2.F5.opExtrude","SWEPT_FACE",FACE,{"disambiguationData":[OSD([sQuery(id+"F4.wireOp",EDGE,"E7.filletArc")])]})]});
            var Q183;
            Q183=makeQuery(id+"Fd9uYAkPvKm23FF_1.2.F5.boolean.opBoolean","INTERSECT",EDGE,{"derivedFrom":[makeQuery(id+"F2.opShell","OFFSET_FACE",FACE,{"disambiguationData":[OSD([sQuery(id+"F0.wireOp",EDGE,"E4")])]}),makeQuery(id+"Fd9uYAkPvKm23FF_1.2.F5.opExtrude","SWEPT_FACE",FACE,{"disambiguationData":[OSD([sQuery(id+"F4.wireOp",EDGE,"E7.filletArc")])]})]});
            var Q184;
            Q184=makeQuery(id+"Fd9uYAkPvKm23FF_1.2.F5.boolean.opBoolean","INTERSECT",EDGE,{"derivedFrom":[makeQuery(id+"F2.opShell","OFFSET_FACE",FACE,{"disambiguationData":[OSD([sQuery(id+"F0.wireOp",EDGE,"E4")])]}),makeQuery(id+"Fd9uYAkPvKm23FF_1.2.F5.opExtrude","SWEPT_FACE",FACE,{"disambiguationData":[OSD([sQuery(id+"F4.wireOp",EDGE,"E8.filletArc")])]})]});
            var Q185;
            Q185=makeQuery(id+"Fd9uYAkPvKm23FF_1.2.F5.boolean.opBoolean","INTERSECT",EDGE,{"derivedFrom":[makeQuery(id+"F1.opRevolve","SWEPT_FACE",FACE,{"disambiguationData":[OSD([sQuery(id+"F0.wireOp",EDGE,"E4")])]}),makeQuery(id+"Fd9uYAkPvKm23FF_1.2.F5.opExtrude","SWEPT_FACE",FACE,{"disambiguationData":[OSD([sQuery(id+"F4.wireOp",EDGE,"E9.filletArc")])]})]});
            var Q186;
            Q186=makeQuery(id+"Fd9uYAkPvKm23FF_1.2.F5.boolean.opBoolean","INTERSECT",EDGE,{"derivedFrom":[makeQuery(id+"F2.opShell","OFFSET_FACE",FACE,{"disambiguationData":[OSD([sQuery(id+"F0.wireOp",EDGE,"E4")])]}),makeQuery(id+"Fd9uYAkPvKm23FF_1.2.F5.opExtrude","SWEPT_FACE",FACE,{"disambiguationData":[OSD([sQuery(id+"F4.wireOp",EDGE,"E9.filletArc")])]})]});
            var Q187;
            Q187=makeQuery(id+"Fd9uYAkPvKm23FF_1.2.F5.boolean.opBoolean","INTERSECT",EDGE,{"derivedFrom":[makeQuery(id+"F1.opRevolve","SWEPT_FACE",FACE,{"disambiguationData":[OSD([sQuery(id+"F0.wireOp",EDGE,"E4")])]}),makeQuery(id+"Fd9uYAkPvKm23FF_1.2.F5.opExtrude","SWEPT_FACE",FACE,{"disambiguationData":[OSD([sQuery(id+"F4.wireOp",EDGE,"E10.filletArc")])]})]});
            var Q188;
            Q188=makeQuery(id+"Fd9uYAkPvKm23FF_1.3.F5.boolean.opBoolean","INTERSECT",EDGE,{"derivedFrom":[makeQuery(id+"F2.opShell","OFFSET_FACE",FACE,{"disambiguationData":[OSD([sQuery(id+"F0.wireOp",EDGE,"E4")])]}),makeQuery(id+"Fd9uYAkPvKm23FF_1.3.F5.opExtrude","SWEPT_FACE",FACE,{"disambiguationData":[OSD([sQuery(id+"F4.wireOp",EDGE,"E7.filletArc")])]})]});
            var Q189;
            Q189=makeQuery(id+"Fd9uYAkPvKm23FF_1.3.F5.boolean.opBoolean","INTERSECT",EDGE,{"derivedFrom":[makeQuery(id+"F1.opRevolve","SWEPT_FACE",FACE,{"disambiguationData":[OSD([sQuery(id+"F0.wireOp",EDGE,"E4")])]}),makeQuery(id+"Fd9uYAkPvKm23FF_1.3.F5.opExtrude","SWEPT_FACE",FACE,{"disambiguationData":[OSD([sQuery(id+"F4.wireOp",EDGE,"E8.filletArc")])]})]});
            var Q190;
            Q190=makeQuery(id+"Fd9uYAkPvKm23FF_1.3.F5.boolean.opBoolean","INTERSECT",EDGE,{"derivedFrom":[makeQuery(id+"F2.opShell","OFFSET_FACE",FACE,{"disambiguationData":[OSD([sQuery(id+"F0.wireOp",EDGE,"E4")])]}),makeQuery(id+"Fd9uYAkPvKm23FF_1.3.F5.opExtrude","SWEPT_FACE",FACE,{"disambiguationData":[OSD([sQuery(id+"F4.wireOp",EDGE,"E8.filletArc")])]})]});
            var Q191;
            Q191=makeQuery(id+"Fd9uYAkPvKm23FF_1.3.F5.boolean.opBoolean","INTERSECT",EDGE,{"derivedFrom":[makeQuery(id+"F1.opRevolve","SWEPT_FACE",FACE,{"disambiguationData":[OSD([sQuery(id+"F0.wireOp",EDGE,"E4")])]}),makeQuery(id+"Fd9uYAkPvKm23FF_1.3.F5.opExtrude","SWEPT_FACE",FACE,{"disambiguationData":[OSD([sQuery(id+"F4.wireOp",EDGE,"E9.filletArc")])]})]});
            var Q192;
            Q192=makeQuery(id+"Fd9uYAkPvKm23FF_1.3.F5.boolean.opBoolean","INTERSECT",EDGE,{"derivedFrom":[makeQuery(id+"F2.opShell","OFFSET_FACE",FACE,{"disambiguationData":[OSD([sQuery(id+"F0.wireOp",EDGE,"E4")])]}),makeQuery(id+"Fd9uYAkPvKm23FF_1.3.F5.opExtrude","SWEPT_FACE",FACE,{"disambiguationData":[OSD([sQuery(id+"F4.wireOp",EDGE,"E9.filletArc")])]})]});
            var Q193;
            Q193=makeQuery(id+"Fd9uYAkPvKm23FF_1.3.F5.boolean.opBoolean","INTERSECT",EDGE,{"derivedFrom":[makeQuery(id+"F2.opShell","OFFSET_FACE",FACE,{"disambiguationData":[OSD([sQuery(id+"F0.wireOp",EDGE,"E4")])]}),makeQuery(id+"Fd9uYAkPvKm23FF_1.3.F5.opExtrude","SWEPT_FACE",FACE,{"disambiguationData":[OSD([sQuery(id+"F4.wireOp",EDGE,"E10.filletArc")])]})]});
            var Q194;
            Q194=makeQuery(id+"Fd9uYAkPvKm23FF_1.4.F5.boolean.opBoolean","INTERSECT",EDGE,{"derivedFrom":[makeQuery(id+"F1.opRevolve","SWEPT_FACE",FACE,{"disambiguationData":[OSD([sQuery(id+"F0.wireOp",EDGE,"E4")])]}),makeQuery(id+"Fd9uYAkPvKm23FF_1.4.F5.opExtrude","SWEPT_FACE",FACE,{"disambiguationData":[OSD([sQuery(id+"F4.wireOp",EDGE,"E7.filletArc")])]})]});
            var Q195;
            Q195=makeQuery(id+"Fd9uYAkPvKm23FF_1.4.F5.boolean.opBoolean","INTERSECT",EDGE,{"derivedFrom":[makeQuery(id+"F1.opRevolve","SWEPT_FACE",FACE,{"disambiguationData":[OSD([sQuery(id+"F0.wireOp",EDGE,"E4")])]}),makeQuery(id+"Fd9uYAkPvKm23FF_1.4.F5.opExtrude","SWEPT_FACE",FACE,{"disambiguationData":[OSD([sQuery(id+"F4.wireOp",EDGE,"E8.filletArc")])]})]});
            var Q196;
            Q196=makeQuery(id+"Fd9uYAkPvKm23FF_1.4.F5.boolean.opBoolean","INTERSECT",EDGE,{"derivedFrom":[makeQuery(id+"F2.opShell","OFFSET_FACE",FACE,{"disambiguationData":[OSD([sQuery(id+"F0.wireOp",EDGE,"E4")])]}),makeQuery(id+"Fd9uYAkPvKm23FF_1.4.F5.opExtrude","SWEPT_FACE",FACE,{"disambiguationData":[OSD([sQuery(id+"F4.wireOp",EDGE,"E8.filletArc")])]})]});
            var Q197;
            Q197=makeQuery(id+"Fd9uYAkPvKm23FF_1.4.F5.boolean.opBoolean","INTERSECT",EDGE,{"derivedFrom":[makeQuery(id+"F1.opRevolve","SWEPT_FACE",FACE,{"disambiguationData":[OSD([sQuery(id+"F0.wireOp",EDGE,"E4")])]}),makeQuery(id+"Fd9uYAkPvKm23FF_1.4.F5.opExtrude","SWEPT_FACE",FACE,{"disambiguationData":[OSD([sQuery(id+"F4.wireOp",EDGE,"E9.filletArc")])]})]});
            var Q198;
            Q198=makeQuery(id+"Fd9uYAkPvKm23FF_1.4.F5.boolean.opBoolean","INTERSECT",EDGE,{"derivedFrom":[makeQuery(id+"F1.opRevolve","SWEPT_FACE",FACE,{"disambiguationData":[OSD([sQuery(id+"F0.wireOp",EDGE,"E4")])]}),makeQuery(id+"Fd9uYAkPvKm23FF_1.4.F5.opExtrude","SWEPT_FACE",FACE,{"disambiguationData":[OSD([sQuery(id+"F4.wireOp",EDGE,"E10.filletArc")])]})]});
            var Q199;
            Q199=makeQuery(id+"Fd9uYAkPvKm23FF_1.4.F5.boolean.opBoolean","INTERSECT",EDGE,{"derivedFrom":[makeQuery(id+"F2.opShell","OFFSET_FACE",FACE,{"disambiguationData":[OSD([sQuery(id+"F0.wireOp",EDGE,"E4")])]}),makeQuery(id+"Fd9uYAkPvKm23FF_1.4.F5.opExtrude","SWEPT_FACE",FACE,{"disambiguationData":[OSD([sQuery(id+"F4.wireOp",EDGE,"E10.filletArc")])]})]});
            var Q200;
            Q200=makeQuery(id+"Fd9uYAkPvKm23FF_1.5.F5.boolean.opBoolean","INTERSECT",EDGE,{"derivedFrom":[makeQuery(id+"F2.opShell","OFFSET_FACE",FACE,{"disambiguationData":[OSD([sQuery(id+"F0.wireOp",EDGE,"E4")])]}),makeQuery(id+"Fd9uYAkPvKm23FF_1.5.F5.opExtrude","SWEPT_FACE",FACE,{"disambiguationData":[OSD([sQuery(id+"F4.wireOp",EDGE,"E8.filletArc")])]})]});
            var Q201;
            Q201=makeQuery(id+"Fd9uYAkPvKm23FF_1.5.F5.boolean.opBoolean","INTERSECT",EDGE,{"derivedFrom":[makeQuery(id+"F1.opRevolve","SWEPT_FACE",FACE,{"disambiguationData":[OSD([sQuery(id+"F0.wireOp",EDGE,"E4")])]}),makeQuery(id+"Fd9uYAkPvKm23FF_1.5.F5.opExtrude","SWEPT_FACE",FACE,{"disambiguationData":[OSD([sQuery(id+"F4.wireOp",EDGE,"E10.filletArc")])]})]});
            var Q202;
            Q202=makeQuery(id+"Fd9uYAkPvKm23FF_1.6.F5.boolean.opBoolean","INTERSECT",EDGE,{"derivedFrom":[makeQuery(id+"F1.opRevolve","SWEPT_FACE",FACE,{"disambiguationData":[OSD([sQuery(id+"F0.wireOp",EDGE,"E4")])]}),makeQuery(id+"Fd9uYAkPvKm23FF_1.6.F5.opExtrude","SWEPT_FACE",FACE,{"disambiguationData":[OSD([sQuery(id+"F4.wireOp",EDGE,"E7.filletArc")])]})]});
            var Q203;
            Q203=makeQuery(id+"Fd9uYAkPvKm23FF_1.6.F5.boolean.opBoolean","INTERSECT",EDGE,{"derivedFrom":[makeQuery(id+"F1.opRevolve","SWEPT_FACE",FACE,{"disambiguationData":[OSD([sQuery(id+"F0.wireOp",EDGE,"E4")])]}),makeQuery(id+"Fd9uYAkPvKm23FF_1.6.F5.opExtrude","SWEPT_FACE",FACE,{"disambiguationData":[OSD([sQuery(id+"F4.wireOp",EDGE,"E8.filletArc")])]})]});
            var Q204;
            Q204=makeQuery(id+"Fd9uYAkPvKm23FF_1.6.F5.boolean.opBoolean","INTERSECT",EDGE,{"derivedFrom":[makeQuery(id+"F1.opRevolve","SWEPT_FACE",FACE,{"disambiguationData":[OSD([sQuery(id+"F0.wireOp",EDGE,"E4")])]}),makeQuery(id+"Fd9uYAkPvKm23FF_1.6.F5.opExtrude","SWEPT_FACE",FACE,{"disambiguationData":[OSD([sQuery(id+"F4.wireOp",EDGE,"E9.filletArc")])]})]});
            var Q205;
            Q205=makeQuery(id+"Fd9uYAkPvKm23FF_1.6.F5.boolean.opBoolean","INTERSECT",EDGE,{"derivedFrom":[makeQuery(id+"F2.opShell","OFFSET_FACE",FACE,{"disambiguationData":[OSD([sQuery(id+"F0.wireOp",EDGE,"E4")])]}),makeQuery(id+"Fd9uYAkPvKm23FF_1.6.F5.opExtrude","SWEPT_FACE",FACE,{"disambiguationData":[OSD([sQuery(id+"F4.wireOp",EDGE,"E9.filletArc")])]})]});
            var Q206;
            Q206=makeQuery(id+"Fd9uYAkPvKm23FF_1.6.F5.boolean.opBoolean","INTERSECT",EDGE,{"derivedFrom":[makeQuery(id+"F1.opRevolve","SWEPT_FACE",FACE,{"disambiguationData":[OSD([sQuery(id+"F0.wireOp",EDGE,"E4")])]}),makeQuery(id+"Fd9uYAkPvKm23FF_1.6.F5.opExtrude","SWEPT_FACE",FACE,{"disambiguationData":[OSD([sQuery(id+"F4.wireOp",EDGE,"E10.filletArc")])]})]});
            var Q207;
            Q207=makeQuery(id+"Fd9uYAkPvKm23FF_1.6.F5.boolean.opBoolean","INTERSECT",EDGE,{"derivedFrom":[makeQuery(id+"F2.opShell","OFFSET_FACE",FACE,{"disambiguationData":[OSD([sQuery(id+"F0.wireOp",EDGE,"E4")])]}),makeQuery(id+"Fd9uYAkPvKm23FF_1.6.F5.opExtrude","SWEPT_FACE",FACE,{"disambiguationData":[OSD([sQuery(id+"F4.wireOp",EDGE,"E10.filletArc")])]})]});
            var Q208;
            Q208=makeQuery(id+"F5.boolean.opBoolean","COPY",FACE,{"derivedFrom":makeQuery(id+"F5.opExtrude","SWEPT_FACE",FACE,{"disambiguationData":[OSD([sQuery(id+"F4.wireOp",EDGE,"E8.filletArc")])]})});
            var Q209;
            Q209=makeQuery(id+"F5.boolean.opBoolean","COPY",EDGE,{"derivedFrom":makeQuery(id+"F5.opExtrude","SWEPT_EDGE",EDGE,{"disambiguationData":[OSD([sQuery(id+"F4.wireOp",EDGE,"E6.top"),sQuery(id+"F4.wireOp",EDGE,"E9.filletArc")])]})});
            var Q210;
            Q210=makeQuery(id+"F5.boolean.opBoolean","COPY",EDGE,{"derivedFrom":makeQuery(id+"F5.opExtrude","SWEPT_EDGE",EDGE,{"disambiguationData":[OSD([sQuery(id+"F4.wireOp",EDGE,"E6.top"),sQuery(id+"F4.wireOp",EDGE,"E10.filletArc")])]})});
            var Q211;
            Q211=makeQuery(id+"F5.boolean.opBoolean","INTERSECT",EDGE,{"derivedFrom":[makeQuery(id+"F2.opShell","OFFSET_FACE",FACE,{"disambiguationData":[OSD([sQuery(id+"F0.wireOp",EDGE,"E4")])]}),makeQuery(id+"F5.opExtrude","SWEPT_FACE",FACE,{"disambiguationData":[OSD([sQuery(id+"F4.wireOp",EDGE,"E6.left")])]})]});
            var Q212;
            Q212=makeQuery(id+"F5.boolean.opBoolean","COPY",EDGE,{"derivedFrom":makeQuery(id+"F5.opExtrude","SWEPT_EDGE",EDGE,{"disambiguationData":[OSD([sQuery(id+"F4.wireOp",EDGE,"E6.left"),sQuery(id+"F4.wireOp",EDGE,"E9.filletArc")])]})});
            var Q213;
            Q213=makeQuery(id+"F5.boolean.opBoolean","INTERSECT",EDGE,{"derivedFrom":[makeQuery(id+"F1.opRevolve","SWEPT_FACE",FACE,{"disambiguationData":[OSD([sQuery(id+"F0.wireOp",EDGE,"E4")])]}),makeQuery(id+"F5.opExtrude","SWEPT_FACE",FACE,{"disambiguationData":[OSD([sQuery(id+"F4.wireOp",EDGE,"E10.filletArc")])]})]});
            var Q214;
            Q214=makeQuery(id+"F5.boolean.opBoolean","INTERSECT",EDGE,{"derivedFrom":[makeQuery(id+"F2.opShell","OFFSET_FACE",FACE,{"disambiguationData":[OSD([sQuery(id+"F0.wireOp",EDGE,"E4")])]}),makeQuery(id+"F5.opExtrude","SWEPT_FACE",FACE,{"disambiguationData":[OSD([sQuery(id+"F4.wireOp",EDGE,"E9.filletArc")])]})]});
            var Q215;
            Q215=makeQuery(id+"F5.boolean.opBoolean","INTERSECT",EDGE,{"derivedFrom":[makeQuery(id+"F2.opShell","OFFSET_FACE",FACE,{"disambiguationData":[OSD([sQuery(id+"F0.wireOp",EDGE,"E4")])]}),makeQuery(id+"F5.opExtrude","SWEPT_FACE",FACE,{"disambiguationData":[OSD([sQuery(id+"F4.wireOp",EDGE,"E8.filletArc")])]})]});
            var Q216;
            Q216=makeQuery(id+"F5.boolean.opBoolean","INTERSECT",EDGE,{"derivedFrom":[makeQuery(id+"F1.opRevolve","SWEPT_FACE",FACE,{"disambiguationData":[OSD([sQuery(id+"F0.wireOp",EDGE,"E4")])]}),makeQuery(id+"F5.opExtrude","SWEPT_FACE",FACE,{"disambiguationData":[OSD([sQuery(id+"F4.wireOp",EDGE,"E6.left")])]})]});
            var Q217;
            Q217=makeQuery(id+"F5.boolean.opBoolean","INTERSECT",EDGE,{"derivedFrom":[makeQuery(id+"F2.opShell","OFFSET_FACE",FACE,{"disambiguationData":[OSD([sQuery(id+"F0.wireOp",EDGE,"E4")])]}),makeQuery(id+"F5.opExtrude","SWEPT_FACE",FACE,{"disambiguationData":[OSD([sQuery(id+"F4.wireOp",EDGE,"E6.top")])]})]});
            var Q218;
            Q218=makeQuery(id+"F5.boolean.opBoolean","COPY",EDGE,{"derivedFrom":makeQuery(id+"F5.opExtrude","SWEPT_EDGE",EDGE,{"disambiguationData":[OSD([sQuery(id+"F4.wireOp",EDGE,"E6.right"),sQuery(id+"F4.wireOp",EDGE,"E10.filletArc")])]})});
            var Q219;
            Q219=makeQuery(id+"Fd9uYAkPvKm23FF_1.2.F5.boolean.opBoolean","COPY",EDGE,{"derivedFrom":makeQuery(id+"Fd9uYAkPvKm23FF_1.2.F5.opExtrude","SWEPT_EDGE",EDGE,{"disambiguationData":[OSD([sQuery(id+"F4.wireOp",EDGE,"E6.right"),sQuery(id+"F4.wireOp",EDGE,"E10.filletArc")])]})});
            var Q220;
            Q220=makeQuery(id+"Fd9uYAkPvKm23FF_1.2.F5.boolean.opBoolean","COPY",EDGE,{"derivedFrom":makeQuery(id+"Fd9uYAkPvKm23FF_1.2.F5.opExtrude","SWEPT_EDGE",EDGE,{"disambiguationData":[OSD([sQuery(id+"F4.wireOp",EDGE,"E6.left"),sQuery(id+"F4.wireOp",EDGE,"E9.filletArc")])]})});
            var Q221;
            Q221=makeQuery(id+"Fd9uYAkPvKm23FF_1.1.F5.boolean.opBoolean","INTERSECT",EDGE,{"derivedFrom":[makeQuery(id+"F2.opShell","OFFSET_FACE",FACE,{"disambiguationData":[OSD([sQuery(id+"F0.wireOp",EDGE,"E4")])]}),makeQuery(id+"Fd9uYAkPvKm23FF_1.1.F5.opExtrude","SWEPT_FACE",FACE,{"disambiguationData":[OSD([sQuery(id+"F4.wireOp",EDGE,"E6.bottom")])]})]});
            var Q222;
            Q222=makeQuery(id+"Fd9uYAkPvKm23FF_1.1.F5.boolean.opBoolean","COPY",EDGE,{"derivedFrom":makeQuery(id+"Fd9uYAkPvKm23FF_1.1.F5.opExtrude","SWEPT_EDGE",EDGE,{"disambiguationData":[OSD([sQuery(id+"F4.wireOp",EDGE,"E6.right"),sQuery(id+"F4.wireOp",EDGE,"E10.filletArc")])]})});
            var Q223;
            Q223=makeQuery(id+"Fd9uYAkPvKm23FF_1.1.F5.boolean.opBoolean","COPY",EDGE,{"derivedFrom":makeQuery(id+"Fd9uYAkPvKm23FF_1.1.F5.opExtrude","SWEPT_EDGE",EDGE,{"disambiguationData":[OSD([sQuery(id+"F4.wireOp",EDGE,"E6.left"),sQuery(id+"F4.wireOp",EDGE,"E9.filletArc")])]})});
            var Q224;
            Q224=makeQuery(id+"Fd9uYAkPvKm23FF_1.1.F5.boolean.opBoolean","COPY",EDGE,{"derivedFrom":makeQuery(id+"Fd9uYAkPvKm23FF_1.1.F5.opExtrude","SWEPT_EDGE",EDGE,{"disambiguationData":[OSD([sQuery(id+"F4.wireOp",EDGE,"E6.top"),sQuery(id+"F4.wireOp",EDGE,"E9.filletArc")])]})});
            var Q225;
            Q225=makeQuery(id+"Fd9uYAkPvKm23FF_1.5.F5.boolean.opBoolean","COPY",EDGE,{"derivedFrom":makeQuery(id+"Fd9uYAkPvKm23FF_1.5.F5.opExtrude","SWEPT_EDGE",EDGE,{"disambiguationData":[OSD([sQuery(id+"F4.wireOp",EDGE,"E6.bottom"),sQuery(id+"F4.wireOp",EDGE,"E8.filletArc")])]})});
            var Q226;
            Q226=makeQuery(id+"Fd9uYAkPvKm23FF_1.5.F5.boolean.opBoolean","COPY",EDGE,{"derivedFrom":makeQuery(id+"Fd9uYAkPvKm23FF_1.5.F5.opExtrude","SWEPT_EDGE",EDGE,{"disambiguationData":[OSD([sQuery(id+"F4.wireOp",EDGE,"E6.top"),sQuery(id+"F4.wireOp",EDGE,"E9.filletArc")])]})});
            var Q227;
            Q227=makeQuery(id+"Fd9uYAkPvKm23FF_1.5.F5.boolean.opBoolean","COPY",EDGE,{"derivedFrom":makeQuery(id+"Fd9uYAkPvKm23FF_1.5.F5.opExtrude","SWEPT_EDGE",EDGE,{"disambiguationData":[OSD([sQuery(id+"F4.wireOp",EDGE,"E6.top"),sQuery(id+"F4.wireOp",EDGE,"E10.filletArc")])]})});
            var Q228;
            Q228=makeQuery(id+"Fd9uYAkPvKm23FF_1.5.F5.boolean.opBoolean","COPY",EDGE,{"derivedFrom":makeQuery(id+"Fd9uYAkPvKm23FF_1.5.F5.opExtrude","SWEPT_EDGE",EDGE,{"disambiguationData":[OSD([sQuery(id+"F4.wireOp",EDGE,"E6.left"),sQuery(id+"F4.wireOp",EDGE,"E8.filletArc")])]})});
            var Q229;
            Q229=makeQuery(id+"Fd9uYAkPvKm23FF_1.5.F5.boolean.opBoolean","COPY",EDGE,{"derivedFrom":makeQuery(id+"Fd9uYAkPvKm23FF_1.5.F5.opExtrude","SWEPT_EDGE",EDGE,{"disambiguationData":[OSD([sQuery(id+"F4.wireOp",EDGE,"E6.right"),sQuery(id+"F4.wireOp",EDGE,"E7.filletArc")])]})});
            var Q230;
            Q230=makeQuery(id+"Fd9uYAkPvKm23FF_1.5.F5.boolean.opBoolean","COPY",FACE,{"derivedFrom":makeQuery(id+"Fd9uYAkPvKm23FF_1.5.F5.opExtrude","SWEPT_FACE",FACE,{"disambiguationData":[OSD([sQuery(id+"F4.wireOp",EDGE,"E9.filletArc")])]})});
            var Q231;
            Q231=makeQuery(id+"Fd9uYAkPvKm23FF_1.5.F5.boolean.opBoolean","COPY",EDGE,{"derivedFrom":makeQuery(id+"Fd9uYAkPvKm23FF_1.5.F5.opExtrude","SWEPT_EDGE",EDGE,{"disambiguationData":[OSD([sQuery(id+"F4.wireOp",EDGE,"E6.right"),sQuery(id+"F4.wireOp",EDGE,"E10.filletArc")])]})});
            var Q232;
            Q232=makeQuery(id+"Fd9uYAkPvKm23FF_1.5.F5.boolean.opBoolean","INTERSECT",EDGE,{"derivedFrom":[makeQuery(id+"F2.opShell","OFFSET_FACE",FACE,{"disambiguationData":[OSD([sQuery(id+"F0.wireOp",EDGE,"E4")])]}),makeQuery(id+"Fd9uYAkPvKm23FF_1.5.F5.opExtrude","SWEPT_FACE",FACE,{"disambiguationData":[OSD([sQuery(id+"F4.wireOp",EDGE,"E6.top")])]})]});
            var Q233;
            Q233=makeQuery(id+"Fd9uYAkPvKm23FF_1.6.F5.boolean.opBoolean","COPY",EDGE,{"derivedFrom":makeQuery(id+"Fd9uYAkPvKm23FF_1.6.F5.opExtrude","SWEPT_EDGE",EDGE,{"disambiguationData":[OSD([sQuery(id+"F4.wireOp",EDGE,"E6.top"),sQuery(id+"F4.wireOp",EDGE,"E9.filletArc")])]})});
            var Q234;
            Q234=makeQuery(id+"Fd9uYAkPvKm23FF_1.6.F5.boolean.opBoolean","COPY",EDGE,{"derivedFrom":makeQuery(id+"Fd9uYAkPvKm23FF_1.6.F5.opExtrude","SWEPT_EDGE",EDGE,{"disambiguationData":[OSD([sQuery(id+"F4.wireOp",EDGE,"E6.top"),sQuery(id+"F4.wireOp",EDGE,"E10.filletArc")])]})});
            var Q235;
            Q235=makeQuery(id+"Fd9uYAkPvKm23FF_1.6.F5.boolean.opBoolean","COPY",EDGE,{"derivedFrom":makeQuery(id+"Fd9uYAkPvKm23FF_1.6.F5.opExtrude","SWEPT_EDGE",EDGE,{"disambiguationData":[OSD([sQuery(id+"F4.wireOp",EDGE,"E6.left"),sQuery(id+"F4.wireOp",EDGE,"E8.filletArc")])]})});
            var Q236;
            Q236=makeQuery(id+"Fd9uYAkPvKm23FF_1.6.F5.boolean.opBoolean","COPY",EDGE,{"derivedFrom":makeQuery(id+"Fd9uYAkPvKm23FF_1.6.F5.opExtrude","SWEPT_EDGE",EDGE,{"disambiguationData":[OSD([sQuery(id+"F4.wireOp",EDGE,"E6.left"),sQuery(id+"F4.wireOp",EDGE,"E9.filletArc")])]})});
            var Q237;
            Q237=makeQuery(id+"Fd9uYAkPvKm23FF_1.6.F5.boolean.opBoolean","INTERSECT",EDGE,{"derivedFrom":[makeQuery(id+"F2.opShell","OFFSET_FACE",FACE,{"disambiguationData":[OSD([sQuery(id+"F0.wireOp",EDGE,"E4")])]}),makeQuery(id+"Fd9uYAkPvKm23FF_1.6.F5.opExtrude","SWEPT_FACE",FACE,{"disambiguationData":[OSD([sQuery(id+"F4.wireOp",EDGE,"E6.top")])]})]});
            var Q238;
            Q238=makeQuery(id+"Fd9uYAkPvKm23FF_1.1.F5.boolean.opBoolean","INTERSECT",EDGE,{"derivedFrom":[makeQuery(id+"F2.opShell","OFFSET_FACE",FACE,{"disambiguationData":[OSD([sQuery(id+"F0.wireOp",EDGE,"E4")])]}),makeQuery(id+"Fd9uYAkPvKm23FF_1.1.F5.opExtrude","SWEPT_FACE",FACE,{"disambiguationData":[OSD([sQuery(id+"F4.wireOp",EDGE,"E7.filletArc")])]})]});
            var Q239;
            Q239=makeQuery(id+"Fd9uYAkPvKm23FF_1.1.F5.boolean.opBoolean","INTERSECT",EDGE,{"derivedFrom":[makeQuery(id+"F2.opShell","OFFSET_FACE",FACE,{"disambiguationData":[OSD([sQuery(id+"F0.wireOp",EDGE,"E4")])]}),makeQuery(id+"Fd9uYAkPvKm23FF_1.1.F5.opExtrude","SWEPT_FACE",FACE,{"disambiguationData":[OSD([sQuery(id+"F4.wireOp",EDGE,"E8.filletArc")])]})]});
            var Q240;
            Q240=makeQuery(id+"Fd9uYAkPvKm23FF_1.1.F5.boolean.opBoolean","INTERSECT",EDGE,{"derivedFrom":[makeQuery(id+"F1.opRevolve","SWEPT_FACE",FACE,{"disambiguationData":[OSD([sQuery(id+"F0.wireOp",EDGE,"E4")])]}),makeQuery(id+"Fd9uYAkPvKm23FF_1.1.F5.opExtrude","SWEPT_FACE",FACE,{"disambiguationData":[OSD([sQuery(id+"F4.wireOp",EDGE,"E10.filletArc")])]})]});
            var Q241;
            Q241=makeQuery(id+"Fd9uYAkPvKm23FF_1.1.F5.boolean.opBoolean","INTERSECT",EDGE,{"derivedFrom":[makeQuery(id+"F2.opShell","OFFSET_FACE",FACE,{"disambiguationData":[OSD([sQuery(id+"F0.wireOp",EDGE,"E4")])]}),makeQuery(id+"Fd9uYAkPvKm23FF_1.1.F5.opExtrude","SWEPT_FACE",FACE,{"disambiguationData":[OSD([sQuery(id+"F4.wireOp",EDGE,"E10.filletArc")])]})]});
            var Q242;
            Q242=makeQuery(id+"Fd9uYAkPvKm23FF_1.2.F5.boolean.opBoolean","INTERSECT",EDGE,{"derivedFrom":[makeQuery(id+"F2.opShell","OFFSET_FACE",FACE,{"disambiguationData":[OSD([sQuery(id+"F0.wireOp",EDGE,"E4")])]}),makeQuery(id+"Fd9uYAkPvKm23FF_1.2.F5.opExtrude","SWEPT_FACE",FACE,{"disambiguationData":[OSD([sQuery(id+"F4.wireOp",EDGE,"E10.filletArc")])]})]});
            var Q243;
            Q243=makeQuery(id+"Fd9uYAkPvKm23FF_1.4.F5.boolean.opBoolean","INTERSECT",EDGE,{"derivedFrom":[makeQuery(id+"F2.opShell","OFFSET_FACE",FACE,{"disambiguationData":[OSD([sQuery(id+"F0.wireOp",EDGE,"E4")])]}),makeQuery(id+"Fd9uYAkPvKm23FF_1.4.F5.opExtrude","SWEPT_FACE",FACE,{"disambiguationData":[OSD([sQuery(id+"F4.wireOp",EDGE,"E7.filletArc")])]})]});
            var Q244;
            Q244=makeQuery(id+"Fd9uYAkPvKm23FF_1.4.F5.boolean.opBoolean","INTERSECT",EDGE,{"derivedFrom":[makeQuery(id+"F2.opShell","OFFSET_FACE",FACE,{"disambiguationData":[OSD([sQuery(id+"F0.wireOp",EDGE,"E4")])]}),makeQuery(id+"Fd9uYAkPvKm23FF_1.4.F5.opExtrude","SWEPT_FACE",FACE,{"disambiguationData":[OSD([sQuery(id+"F4.wireOp",EDGE,"E9.filletArc")])]})]});
            var Q245;
            Q245=makeQuery(id+"Fd9uYAkPvKm23FF_1.5.F5.boolean.opBoolean","INTERSECT",EDGE,{"derivedFrom":[makeQuery(id+"F1.opRevolve","SWEPT_FACE",FACE,{"disambiguationData":[OSD([sQuery(id+"F0.wireOp",EDGE,"E4")])]}),makeQuery(id+"Fd9uYAkPvKm23FF_1.5.F5.opExtrude","SWEPT_FACE",FACE,{"disambiguationData":[OSD([sQuery(id+"F4.wireOp",EDGE,"E7.filletArc")])]})]});
            var Q246;
            Q246=makeQuery(id+"Fd9uYAkPvKm23FF_1.5.F5.boolean.opBoolean","INTERSECT",EDGE,{"derivedFrom":[makeQuery(id+"F2.opShell","OFFSET_FACE",FACE,{"disambiguationData":[OSD([sQuery(id+"F0.wireOp",EDGE,"E4")])]}),makeQuery(id+"Fd9uYAkPvKm23FF_1.5.F5.opExtrude","SWEPT_FACE",FACE,{"disambiguationData":[OSD([sQuery(id+"F4.wireOp",EDGE,"E7.filletArc")])]})]});
            var Q247;
            Q247=makeQuery(id+"Fd9uYAkPvKm23FF_1.5.F5.boolean.opBoolean","INTERSECT",EDGE,{"derivedFrom":[makeQuery(id+"F1.opRevolve","SWEPT_FACE",FACE,{"disambiguationData":[OSD([sQuery(id+"F0.wireOp",EDGE,"E4")])]}),makeQuery(id+"Fd9uYAkPvKm23FF_1.5.F5.opExtrude","SWEPT_FACE",FACE,{"disambiguationData":[OSD([sQuery(id+"F4.wireOp",EDGE,"E8.filletArc")])]})]});
            var Q248;
            Q248=makeQuery(id+"Fd9uYAkPvKm23FF_1.5.F5.boolean.opBoolean","INTERSECT",EDGE,{"derivedFrom":[makeQuery(id+"F1.opRevolve","SWEPT_FACE",FACE,{"disambiguationData":[OSD([sQuery(id+"F0.wireOp",EDGE,"E4")])]}),makeQuery(id+"Fd9uYAkPvKm23FF_1.5.F5.opExtrude","SWEPT_FACE",FACE,{"disambiguationData":[OSD([sQuery(id+"F4.wireOp",EDGE,"E9.filletArc")])]})]});
            var Q249;
            Q249=makeQuery(id+"Fd9uYAkPvKm23FF_1.5.F5.boolean.opBoolean","INTERSECT",EDGE,{"derivedFrom":[makeQuery(id+"F2.opShell","OFFSET_FACE",FACE,{"disambiguationData":[OSD([sQuery(id+"F0.wireOp",EDGE,"E4")])]}),makeQuery(id+"Fd9uYAkPvKm23FF_1.5.F5.opExtrude","SWEPT_FACE",FACE,{"disambiguationData":[OSD([sQuery(id+"F4.wireOp",EDGE,"E9.filletArc")])]})]});
            var Q250;
            Q250=makeQuery(id+"Fd9uYAkPvKm23FF_1.5.F5.boolean.opBoolean","INTERSECT",EDGE,{"derivedFrom":[makeQuery(id+"F2.opShell","OFFSET_FACE",FACE,{"disambiguationData":[OSD([sQuery(id+"F0.wireOp",EDGE,"E4")])]}),makeQuery(id+"Fd9uYAkPvKm23FF_1.5.F5.opExtrude","SWEPT_FACE",FACE,{"disambiguationData":[OSD([sQuery(id+"F4.wireOp",EDGE,"E10.filletArc")])]})]});
            var Q251;
            Q251=makeQuery(id+"F5.boolean.opBoolean","COPY",EDGE,{"derivedFrom":makeQuery(id+"F5.opExtrude","SWEPT_EDGE",EDGE,{"disambiguationData":[OSD([sQuery(id+"F4.wireOp",EDGE,"E6.bottom"),sQuery(id+"F4.wireOp",EDGE,"E8.filletArc")])]})});
            var Q252;
            Q252=makeQuery(id+"F5.boolean.opBoolean","COPY",EDGE,{"derivedFrom":makeQuery(id+"F5.opExtrude","SWEPT_EDGE",EDGE,{"disambiguationData":[OSD([sQuery(id+"F4.wireOp",EDGE,"E6.left"),sQuery(id+"F4.wireOp",EDGE,"E8.filletArc")])]})});
            var Q253;
            Q253=makeQuery(id+"F5.boolean.opBoolean","INTERSECT",EDGE,{"derivedFrom":[makeQuery(id+"F1.opRevolve","SWEPT_FACE",FACE,{"disambiguationData":[OSD([sQuery(id+"F0.wireOp",EDGE,"E4")])]}),makeQuery(id+"F5.opExtrude","SWEPT_FACE",FACE,{"disambiguationData":[OSD([sQuery(id+"F4.wireOp",EDGE,"E8.filletArc")])]})]});
            var Q254;
            Q254=makeQuery(id+"Fd9uYAkPvKm23FF_1.5.F5.boolean.opBoolean","COPY",EDGE,{"derivedFrom":makeQuery(id+"Fd9uYAkPvKm23FF_1.5.F5.opExtrude","SWEPT_EDGE",EDGE,{"disambiguationData":[OSD([sQuery(id+"F4.wireOp",EDGE,"E6.bottom"),sQuery(id+"F4.wireOp",EDGE,"E7.filletArc")])]})});
            var Q255;
            Q255=makeQuery(id+"Fd9uYAkPvKm23FF_1.5.F5.boolean.opBoolean","COPY",EDGE,{"derivedFrom":makeQuery(id+"Fd9uYAkPvKm23FF_1.5.F5.opExtrude","SWEPT_EDGE",EDGE,{"disambiguationData":[OSD([sQuery(id+"F4.wireOp",EDGE,"E6.left"),sQuery(id+"F4.wireOp",EDGE,"E9.filletArc")])]})});
            fillet(context, id + "F6", {"entities" : qUnion([Q0, Q1, Q2, Q3, Q4, Q5, Q6, Q7, Q8, Q9, Q10, Q11, Q12, Q13, Q14, Q15, Q16, Q17, Q18, Q19, Q20, Q21, Q22, Q23, Q24, Q25, Q26, Q27, Q28, Q29, Q30, Q31, Q32, Q33, Q34, Q35, Q36, Q37, Q38, Q39, Q40, Q41, Q42, Q43, Q44, Q45, Q46, Q47, Q48, Q49, Q50, Q51, Q52, Q53, Q54, Q55, Q56, Q57, Q58, Q59, Q60, Q61, Q62, Q63, Q64, Q65, Q66, Q67, Q68, Q69, Q70, Q71, Q72, Q73, Q74, Q75, Q76, Q77, Q78, Q79, Q80, Q81, Q82, Q83, Q84, Q85, Q86, Q87, Q88, Q89, Q90, Q91, Q92, Q93, Q94, Q95, Q96, Q97, Q98, Q99, Q100, Q101, Q102, Q103, Q104, Q105, Q106, Q107, Q108, Q109, Q110, Q111, Q112, Q113, Q114, Q115, Q116, Q117, Q118, Q119, Q120, Q121, Q122, Q123, Q124, Q125, Q126, Q127, Q128, Q129, Q130, Q131, Q132, Q133, Q134, Q135, Q136, Q137, Q138, Q139, Q140, Q141, Q142, Q143, Q144, Q145, Q146, Q147, Q148, Q149, Q150, Q151, Q152, Q153, Q154, Q155, Q156, Q157, Q158, Q159, Q160, Q161, Q162, Q163, Q164, Q165, Q166, Q167, Q168, Q169, Q170, Q171, Q172, Q173, Q174, Q175, Q176, Q177, Q178, Q179, Q180, Q181, Q182, Q183, Q184, Q185, Q186, Q187, Q188, Q189, Q190, Q191, Q192, Q193, Q194, Q195, Q196, Q197, Q198, Q199, Q200, Q201, Q202, Q203, Q204, Q205, Q206, Q207, Q208, Q209, Q210, Q211, Q212, Q213, Q214, Q215, Q216, Q217, Q218, Q219, Q220, Q221, Q222, Q223, Q224, Q225, Q226, Q227, Q228, Q229, Q230, Q231, Q232, Q233, Q234, Q235, Q236, Q237, Q238, Q239, Q240, Q241, Q242, Q243, Q244, Q245, Q246, Q247, Q248, Q249, Q250, Q251, Q252, Q253, Q254, Q255]), "radius" : 0.15 * mm, "tangentPropagation" : true, "allowEdgeOverflow" : false});
        }
    });
